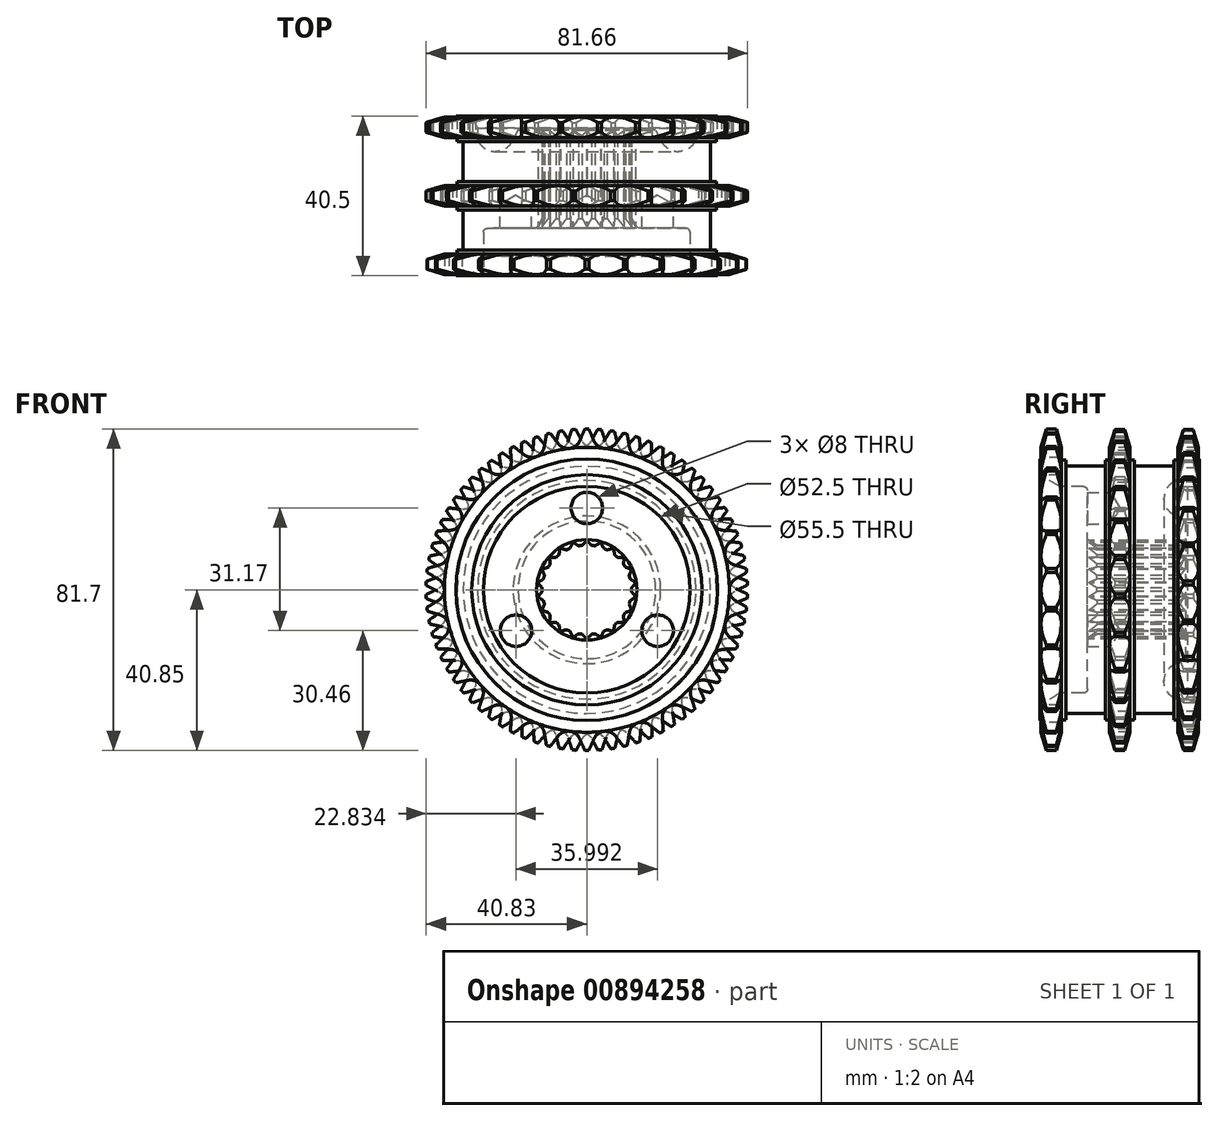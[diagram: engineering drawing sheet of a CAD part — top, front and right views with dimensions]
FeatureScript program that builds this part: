
annotation { "Feature Type Name" : "Feature", "Feature Type Description" : "" }
export const myFeature = defineFeature(function(context is Context, id is Id, definition is map)
    precondition{}
    {
        {
            var Q0;
            Q0=qCreatedBy(makeId("Right.planeOp"),FACE);
            var sketch = newSketch(context, id + "F0", { "sketchPlane" : qUnion([Q0])});
            skLineSegment(sketch, "E0", {"start": v(0, 0) * mm, "end": v(40.5, 0) * mm, "construction": true});
            skLineSegment(sketch, "E1", {"start": v(0, 29.25) * mm, "end": v(0, 33.25) * mm});
            skLineSegment(sketch, "E2", {"start": v(0, 33.25) * mm, "end": v(0.25, 33.25) * mm});
            skLineSegment(sketch, "E3", {"start": v(0.25, 33.25) * mm, "end": v(0.25, 36.2) * mm});
            skLineSegment(sketch, "E4", {"start": v(40.5, 29.25) * mm, "end": v(40.5, 33.25) * mm});
            skLineSegment(sketch, "E5", {"start": v(40.5, 33.25) * mm, "end": v(40.25, 33.25) * mm});
            skLineSegment(sketch, "E6", {"start": v(40.25, 33.25) * mm, "end": v(40.25, 36.2) * mm});
            skLineSegment(sketch, "E7", {"start": v(5, 26.25) * mm, "end": v(0, 29.25) * mm});
            skLineSegment(sketch, "E8", {"start": v(5, 26.25) * mm, "end": v(11, 26.25) * mm});
            skLineSegment(sketch, "E9", {"start": v(12, 25.25) * mm, "end": v(12, 12.75) * mm});
            skLineSegment(sketch, "E10", {"start": v(14.5, 11.35) * mm, "end": v(12, 12.75) * mm});
            skLineSegment(sketch, "E11", {"start": v(37, 17.5) * mm, "end": v(37, 12.75) * mm});
            skLineSegment(sketch, "E12", {"start": v(37, 12.75) * mm, "end": v(35.6, 11.35) * mm});
            skLineSegment(sketch, "E13", {"start": v(14.5, 11.35) * mm, "end": v(35.6, 11.35) * mm});
            skLineSegment(sketch, "E14", {"start": v(40.5, 29.25) * mm, "end": v(37.5, 27.75) * mm});
            skLineSegment(sketch, "E15", {"start": v(34.5, 27.75) * mm, "end": v(37.5, 27.75) * mm});
            skArc(sketch, "E16", {"start": v(34.5, 27.75) * mm, "mid": v(31.5, 23.25) * mm, "end": v(34.5, 18.75) * mm});
            skLineSegment(sketch, "E17", {"start": v(34.5, 18.75) * mm, "end": v(37, 17.5) * mm});
            skLineSegment(sketch, "E18", {"start": v(38.9, 40.85) * mm, "end": v(36.4, 40.85) * mm});
            skLineSegment(sketch, "E19", {"start": v(1.6, 40.85) * mm, "end": v(4.1, 40.85) * mm});
            skLineSegment(sketch, "E20", {"start": v(21.5, 40.85) * mm, "end": v(19, 40.85) * mm});
            skLineSegment(sketch, "E21", {"start": v(36.4, 40.85) * mm, "end": v(35.05, 36.2) * mm});
            skLineSegment(sketch, "E22", {"start": v(38.9, 40.85) * mm, "end": v(40.25, 36.2) * mm});
            skLineSegment(sketch, "E23", {"start": v(19, 40.85) * mm, "end": v(17.65, 36.2) * mm});
            skLineSegment(sketch, "E24", {"start": v(21.5, 40.85) * mm, "end": v(22.85, 36.2) * mm});
            skLineSegment(sketch, "E25", {"start": v(1.6, 40.85) * mm, "end": v(0.25, 36.2) * mm});
            skLineSegment(sketch, "E26", {"start": v(4.1, 40.85) * mm, "end": v(5.45, 36.2) * mm});
            skLineSegment(sketch, "E27", {"start": v(35.05, 33) * mm, "end": v(34, 33) * mm});
            skLineSegment(sketch, "E28", {"start": v(23.9, 33) * mm, "end": v(22.85, 33) * mm});
            skLineSegment(sketch, "E29", {"start": v(17.65, 33) * mm, "end": v(16.6, 33) * mm});
            skLineSegment(sketch, "E30", {"start": v(6.5, 33) * mm, "end": v(5.45, 33) * mm});
            skLineSegment(sketch, "E31", {"start": v(5.45, 36.2) * mm, "end": v(5.45, 33) * mm});
            skLineSegment(sketch, "E32", {"start": v(17.65, 36.2) * mm, "end": v(17.65, 33) * mm});
            skLineSegment(sketch, "E33", {"start": v(22.85, 36.2) * mm, "end": v(22.85, 33) * mm});
            skLineSegment(sketch, "E34", {"start": v(35.05, 36.2) * mm, "end": v(35.05, 33) * mm});
            skLineSegment(sketch, "E35", {"start": v(23.9, 33) * mm, "end": v(23.9, 31.4) * mm});
            skLineSegment(sketch, "E36", {"start": v(16.6, 33) * mm, "end": v(16.6, 31.4) * mm});
            skLineSegment(sketch, "E37", {"start": v(34, 33) * mm, "end": v(34, 31.4) * mm});
            skLineSegment(sketch, "E38", {"start": v(6.5, 33) * mm, "end": v(6.5, 31.4) * mm});
            skLineSegment(sketch, "E39", {"start": v(23.9, 31.4) * mm, "end": v(34, 31.4) * mm});
            skLineSegment(sketch, "E40", {"start": v(16.6, 31.4) * mm, "end": v(6.5, 31.4) * mm});
            skLineSegment(sketch, "E41", {"start": v(0, 29.25) * mm, "end": v(0, 0) * mm, "construction": true});
            skLineSegment(sketch, "E42", {"start": v(0.25, 36.2) * mm, "end": v(5.45, 36.2) * mm, "construction": true});
            skLineSegment(sketch, "E43", {"start": v(17.65, 36.2) * mm, "end": v(22.85, 36.2) * mm, "construction": true});
            skLineSegment(sketch, "E44", {"start": v(35.05, 36.2) * mm, "end": v(40.25, 36.2) * mm, "construction": true});
            skLineSegment(sketch, "E45", {"start": v(4.1, 40.85) * mm, "end": v(19, 40.85) * mm, "construction": true});
            skLineSegment(sketch, "E46", {"start": v(21.5, 40.85) * mm, "end": v(36.4, 40.85) * mm, "construction": true});
            skPoint(sketch, "E47.visualSharp", {"position": v(12, 26.25) * mm});
            skArc(sketch, "E47.filletArc", {"start": v(12, 25.25) * mm, "mid": v(11.7, 25.96) * mm, "end": v(11, 26.25) * mm});
            skSolve(sketch);
        }
        {
            var Q0;
            Q0=makeQuery(id+"F0.imprint","IMPRINT",FACE,{"disambiguationData":[TD([[makeQuery(id+"F0.imprint","IMPRINT",EDGE,{"derivedFrom":sQuery(id+"F0.wireOp",EDGE,"E1")}),-1.0]])]});
            var Q1;
            Q1=sQuery(id+"F0.wireOp",EDGE,"E0");
            revolve(context, id + "F1", {"surfaceOperationType" : NewSurfaceOperationType.NEW, "entities" : qUnion([Q0]), "axis" : qUnion([Q1]), "revolveType" : RevolveType.FULL});
        }
        {
            var Q0;
            Q0=makeQuery(id+"F1.opRevolve","SWEPT_FACE",FACE,{"disambiguationData":[OSD([sQuery(id+"F0.wireOp",EDGE,"E9")])]});
            var sketch = newSketch(context, id + "F2", { "sketchPlane" : qUnion([Q0])});
            skCircle(sketch, "E48", {"center": v(0, 20.78) * mm, "radius": 4 * mm});
            skLineSegment(sketch, "E49", {"start": v(0, 0) * mm, "end": v(0, 20.78) * mm, "construction": true});
            skCircle(sketch, "E50.1.0", {"center": v(-18, -10.39) * mm, "radius": 4 * mm});
            skCircle(sketch, "E50.2.0", {"center": v(18, -10.4) * mm, "radius": 4 * mm});
            skPoint(sketch, "E50.center", {"position": v(0, 0) * mm});
            skSolve(sketch);
        }
        {
            var Q0;
            Q0=sQuery(id+"F2.wireOp",VERTEX,"E49.end");
            var Q1;
            Q1=sQuery(id+"F2.wireOp",VERTEX,"E50.2.0.center");
            var Q2;
            Q2=sQuery(id+"F2.wireOp",VERTEX,"E50.1.0.center");
            var Q3;
            Q3=makeQuery(id+"F1.opRevolve","SWEPT_BODY",BODY,{"disambiguationData":[OSD([sQuery(id+"F0.wireOp",EDGE,"E1"),sQuery(id+"F0.wireOp",EDGE,"E2"),sQuery(id+"F0.wireOp",EDGE,"E3"),sQuery(id+"F0.wireOp",EDGE,"E4"),sQuery(id+"F0.wireOp",EDGE,"E5"),sQuery(id+"F0.wireOp",EDGE,"E6"),sQuery(id+"F0.wireOp",EDGE,"E7"),sQuery(id+"F0.wireOp",EDGE,"E8"),sQuery(id+"F0.wireOp",EDGE,"E9"),sQuery(id+"F0.wireOp",EDGE,"E10"),sQuery(id+"F0.wireOp",EDGE,"E11"),sQuery(id+"F0.wireOp",EDGE,"E12"),sQuery(id+"F0.wireOp",EDGE,"E13"),sQuery(id+"F0.wireOp",EDGE,"E14"),sQuery(id+"F0.wireOp",EDGE,"E15"),sQuery(id+"F0.wireOp",EDGE,"E16"),sQuery(id+"F0.wireOp",EDGE,"E17"),sQuery(id+"F0.wireOp",EDGE,"E18"),sQuery(id+"F0.wireOp",EDGE,"E19"),sQuery(id+"F0.wireOp",EDGE,"E20"),sQuery(id+"F0.wireOp",EDGE,"E21"),sQuery(id+"F0.wireOp",EDGE,"E22"),sQuery(id+"F0.wireOp",EDGE,"E23"),sQuery(id+"F0.wireOp",EDGE,"E24"),sQuery(id+"F0.wireOp",EDGE,"E25"),sQuery(id+"F0.wireOp",EDGE,"E26"),sQuery(id+"F0.wireOp",EDGE,"E27"),sQuery(id+"F0.wireOp",EDGE,"E28"),sQuery(id+"F0.wireOp",EDGE,"E29"),sQuery(id+"F0.wireOp",EDGE,"E30"),sQuery(id+"F0.wireOp",EDGE,"E31"),sQuery(id+"F0.wireOp",EDGE,"E32"),sQuery(id+"F0.wireOp",EDGE,"E33"),sQuery(id+"F0.wireOp",EDGE,"E34"),sQuery(id+"F0.wireOp",EDGE,"E35"),sQuery(id+"F0.wireOp",EDGE,"E36"),sQuery(id+"F0.wireOp",EDGE,"E37"),sQuery(id+"F0.wireOp",EDGE,"E38"),sQuery(id+"F0.wireOp",EDGE,"E39"),sQuery(id+"F0.wireOp",EDGE,"E40")])]});
            hole(context, id + "F3", {"style" : HoleStyle.SIMPLE, "endStyle" : HoleEndStyle.BLIND, "holeDiameter" : 8 * mm, "majorDiameter" : 5 * mm, "holeDepth" : 6 * mm, "isTappedThrough" : true, "tappedDepth" : 12 * mm, "tapClearance" : 3, "locations" : qUnion([Q0, Q1, Q2]), "scope" : qUnion([Q3]), "startStyle" : HoleStartStyle.SKETCH});
        }
        {
            var Q0;
            Q0=makeQuery(id+"F1.opRevolve","SWEPT_FACE",FACE,{"disambiguationData":[OSD([sQuery(id+"F0.wireOp",EDGE,"E9")])]});
            var sketch = newSketch(context, id + "F4", { "sketchPlane" : qUnion([Q0])});
            skArc(sketch, "E51", {"start": v(0.05, 12.5) * mm, "mid": v(0.03, 12.5) * mm, "end": v(0, 12.5) * mm});
            skArc(sketch, "E52", {"start": v(1.62, 11.23) * mm, "mid": v(1.4, 11.26) * mm, "end": v(1.17, 11.29) * mm});
            skLineSegment(sketch, "E53", {"start": v(1.17, 11.29) * mm, "end": v(0.05, 12.5) * mm});
            skArc(sketch, "E54", {"start": v(0, 12.5) * mm, "mid": v(-0.03, 12.5) * mm, "end": v(-0.05, 12.5) * mm});
            skArc(sketch, "E55", {"start": v(-1.17, 11.29) * mm, "mid": v(-1.4, 11.26) * mm, "end": v(-1.62, 11.23) * mm});
            skLineSegment(sketch, "E56", {"start": v(-1.17, 11.29) * mm, "end": v(-0.05, 12.5) * mm});
            skArc(sketch, "E57", {"start": v(-3.47, 12) * mm, "mid": v(-3.5, 12) * mm, "end": v(-3.52, 12) * mm});
            skArc(sketch, "E58", {"start": v(-1.62, 11.23) * mm, "mid": v(-1.84, 11.2) * mm, "end": v(-2.06, 11.16) * mm});
            skLineSegment(sketch, "E59", {"start": v(-2.06, 11.16) * mm, "end": v(-3.47, 12) * mm});
            skArc(sketch, "E60", {"start": v(-3.52, 12) * mm, "mid": v(-3.55, 11.99) * mm, "end": v(-3.57, 11.98) * mm});
            skArc(sketch, "E61", {"start": v(-4.3, 10.5) * mm, "mid": v(-4.5, 10.42) * mm, "end": v(-4.71, 10.32) * mm});
            skLineSegment(sketch, "E62", {"start": v(-4.3, 10.5) * mm, "end": v(-3.57, 11.98) * mm});
            skArc(sketch, "E63", {"start": v(-6.72, 10.54) * mm, "mid": v(-6.74, 10.53) * mm, "end": v(-6.76, 10.52) * mm});
            skArc(sketch, "E64", {"start": v(-4.71, 10.32) * mm, "mid": v(-4.92, 10.23) * mm, "end": v(-5.12, 10.13) * mm});
            skLineSegment(sketch, "E65", {"start": v(-5.12, 10.13) * mm, "end": v(-6.72, 10.54) * mm});
            skArc(sketch, "E66", {"start": v(-6.76, 10.52) * mm, "mid": v(-6.78, 10.5) * mm, "end": v(-6.8, 10.49) * mm});
            skArc(sketch, "E67", {"start": v(-7.09, 8.87) * mm, "mid": v(-7.26, 8.72) * mm, "end": v(-7.43, 8.58) * mm});
            skLineSegment(sketch, "E68", {"start": v(-7.09, 8.87) * mm, "end": v(-6.8, 10.49) * mm});
            skArc(sketch, "E69", {"start": v(-9.41, 8.22) * mm, "mid": v(-9.43, 8.2) * mm, "end": v(-9.45, 8.19) * mm});
            skArc(sketch, "E70", {"start": v(-7.43, 8.58) * mm, "mid": v(-7.6, 8.43) * mm, "end": v(-7.77, 8.28) * mm});
            skLineSegment(sketch, "E71", {"start": v(-7.77, 8.28) * mm, "end": v(-9.41, 8.22) * mm});
            skArc(sketch, "E72", {"start": v(-9.45, 8.19) * mm, "mid": v(-9.46, 8.17) * mm, "end": v(-9.48, 8.15) * mm});
            skArc(sketch, "E73", {"start": v(-9.3, 6.51) * mm, "mid": v(-9.42, 6.32) * mm, "end": v(-9.55, 6.14) * mm});
            skLineSegment(sketch, "E74", {"start": v(-9.3, 6.51) * mm, "end": v(-9.48, 8.15) * mm});
            skArc(sketch, "E75", {"start": v(-11.35, 5.24) * mm, "mid": v(-11.36, 5.22) * mm, "end": v(-11.37, 5.2) * mm});
            skArc(sketch, "E76", {"start": v(-9.55, 6.14) * mm, "mid": v(-9.67, 5.95) * mm, "end": v(-9.78, 5.75) * mm});
            skLineSegment(sketch, "E77", {"start": v(-9.78, 5.75) * mm, "end": v(-11.35, 5.24) * mm});
            skArc(sketch, "E78", {"start": v(-11.37, 5.2) * mm, "mid": v(-11.38, 5.17) * mm, "end": v(-11.4, 5.15) * mm});
            skArc(sketch, "E79", {"start": v(-10.75, 3.63) * mm, "mid": v(-10.82, 3.41) * mm, "end": v(-10.9, 3.2) * mm});
            skLineSegment(sketch, "E80", {"start": v(-10.75, 3.63) * mm, "end": v(-11.4, 5.15) * mm});
            skArc(sketch, "E81", {"start": v(-12.37, 1.83) * mm, "mid": v(-12.37, 1.8) * mm, "end": v(-12.37, 1.78) * mm});
            skArc(sketch, "E82", {"start": v(-10.9, 3.2) * mm, "mid": v(-10.95, 2.98) * mm, "end": v(-11, 2.76) * mm});
            skLineSegment(sketch, "E83", {"start": v(-11, 2.76) * mm, "end": v(-12.37, 1.83) * mm});
            skArc(sketch, "E84", {"start": v(-12.37, 1.78) * mm, "mid": v(-12.38, 1.75) * mm, "end": v(-12.38, 1.73) * mm});
            skArc(sketch, "E85", {"start": v(-11.34, 0.45) * mm, "mid": v(-11.35, 0.23) * mm, "end": v(-11.35, 0) * mm});
            skLineSegment(sketch, "E86", {"start": v(-11.34, 0.45) * mm, "end": v(-12.38, 1.73) * mm});
            skArc(sketch, "E87", {"start": v(-12.38, -1.73) * mm, "mid": v(-12.38, -1.75) * mm, "end": v(-12.37, -1.78) * mm});
            skArc(sketch, "E88", {"start": v(-11.35, 0) * mm, "mid": v(-11.35, -0.23) * mm, "end": v(-11.34, -0.45) * mm});
            skLineSegment(sketch, "E89", {"start": v(-11.34, -0.45) * mm, "end": v(-12.38, -1.73) * mm});
            skArc(sketch, "E90", {"start": v(-12.37, -1.78) * mm, "mid": v(-12.37, -1.8) * mm, "end": v(-12.37, -1.83) * mm});
            skArc(sketch, "E91", {"start": v(-11, -2.76) * mm, "mid": v(-10.95, -2.98) * mm, "end": v(-10.9, -3.2) * mm});
            skLineSegment(sketch, "E92", {"start": v(-11, -2.76) * mm, "end": v(-12.37, -1.83) * mm});
            skArc(sketch, "E93", {"start": v(-11.4, -5.15) * mm, "mid": v(-11.38, -5.17) * mm, "end": v(-11.37, -5.2) * mm});
            skArc(sketch, "E94", {"start": v(-10.9, -3.2) * mm, "mid": v(-10.82, -3.41) * mm, "end": v(-10.75, -3.63) * mm});
            skLineSegment(sketch, "E95", {"start": v(-10.75, -3.63) * mm, "end": v(-11.4, -5.15) * mm});
            skArc(sketch, "E96", {"start": v(-11.37, -5.2) * mm, "mid": v(-11.36, -5.22) * mm, "end": v(-11.35, -5.24) * mm});
            skArc(sketch, "E97", {"start": v(-9.78, -5.75) * mm, "mid": v(-9.67, -5.95) * mm, "end": v(-9.55, -6.14) * mm});
            skLineSegment(sketch, "E98", {"start": v(-9.78, -5.75) * mm, "end": v(-11.35, -5.24) * mm});
            skArc(sketch, "E99", {"start": v(-9.48, -8.15) * mm, "mid": v(-9.46, -8.17) * mm, "end": v(-9.45, -8.19) * mm});
            skArc(sketch, "E100", {"start": v(-9.55, -6.14) * mm, "mid": v(-9.42, -6.32) * mm, "end": v(-9.3, -6.51) * mm});
            skLineSegment(sketch, "E101", {"start": v(-9.3, -6.51) * mm, "end": v(-9.48, -8.15) * mm});
            skArc(sketch, "E102", {"start": v(-9.45, -8.19) * mm, "mid": v(-9.43, -8.2) * mm, "end": v(-9.41, -8.22) * mm});
            skArc(sketch, "E103", {"start": v(-7.77, -8.28) * mm, "mid": v(-7.6, -8.43) * mm, "end": v(-7.43, -8.58) * mm});
            skLineSegment(sketch, "E104", {"start": v(-7.77, -8.28) * mm, "end": v(-9.41, -8.22) * mm});
            skArc(sketch, "E105", {"start": v(-6.8, -10.49) * mm, "mid": v(-6.78, -10.5) * mm, "end": v(-6.76, -10.52) * mm});
            skArc(sketch, "E106", {"start": v(-7.43, -8.58) * mm, "mid": v(-7.26, -8.72) * mm, "end": v(-7.09, -8.87) * mm});
            skLineSegment(sketch, "E107", {"start": v(-7.09, -8.87) * mm, "end": v(-6.8, -10.49) * mm});
            skArc(sketch, "E108", {"start": v(-6.76, -10.52) * mm, "mid": v(-6.74, -10.53) * mm, "end": v(-6.72, -10.54) * mm});
            skArc(sketch, "E109", {"start": v(-5.12, -10.13) * mm, "mid": v(-4.92, -10.23) * mm, "end": v(-4.71, -10.32) * mm});
            skLineSegment(sketch, "E110", {"start": v(-5.12, -10.13) * mm, "end": v(-6.72, -10.54) * mm});
            skArc(sketch, "E111", {"start": v(-3.57, -11.98) * mm, "mid": v(-3.55, -11.99) * mm, "end": v(-3.52, -12) * mm});
            skArc(sketch, "E112", {"start": v(-4.71, -10.32) * mm, "mid": v(-4.5, -10.42) * mm, "end": v(-4.3, -10.5) * mm});
            skLineSegment(sketch, "E113", {"start": v(-4.3, -10.5) * mm, "end": v(-3.57, -11.98) * mm});
            skArc(sketch, "E114", {"start": v(-3.52, -12) * mm, "mid": v(-3.5, -12) * mm, "end": v(-3.47, -12) * mm});
            skArc(sketch, "E115", {"start": v(-2.06, -11.16) * mm, "mid": v(-1.84, -11.2) * mm, "end": v(-1.62, -11.23) * mm});
            skLineSegment(sketch, "E116", {"start": v(-2.06, -11.16) * mm, "end": v(-3.47, -12) * mm});
            skArc(sketch, "E117", {"start": v(-0.05, -12.5) * mm, "mid": v(-0.03, -12.5) * mm, "end": v(0, -12.5) * mm});
            skArc(sketch, "E118", {"start": v(-1.62, -11.23) * mm, "mid": v(-1.4, -11.26) * mm, "end": v(-1.17, -11.29) * mm});
            skLineSegment(sketch, "E119", {"start": v(-1.17, -11.29) * mm, "end": v(-0.05, -12.5) * mm});
            skArc(sketch, "E120", {"start": v(0, -12.5) * mm, "mid": v(0.03, -12.5) * mm, "end": v(0.05, -12.5) * mm});
            skArc(sketch, "E121", {"start": v(1.17, -11.29) * mm, "mid": v(1.4, -11.26) * mm, "end": v(1.62, -11.23) * mm});
            skLineSegment(sketch, "E122", {"start": v(1.17, -11.29) * mm, "end": v(0.05, -12.5) * mm});
            skArc(sketch, "E123", {"start": v(3.47, -12) * mm, "mid": v(3.5, -12) * mm, "end": v(3.52, -12) * mm});
            skArc(sketch, "E124", {"start": v(1.62, -11.23) * mm, "mid": v(1.84, -11.2) * mm, "end": v(2.06, -11.16) * mm});
            skLineSegment(sketch, "E125", {"start": v(2.06, -11.16) * mm, "end": v(3.47, -12) * mm});
            skArc(sketch, "E126", {"start": v(3.52, -12) * mm, "mid": v(3.55, -11.99) * mm, "end": v(3.57, -11.98) * mm});
            skArc(sketch, "E127", {"start": v(4.3, -10.5) * mm, "mid": v(4.5, -10.42) * mm, "end": v(4.71, -10.32) * mm});
            skLineSegment(sketch, "E128", {"start": v(4.3, -10.5) * mm, "end": v(3.57, -11.98) * mm});
            skArc(sketch, "E129", {"start": v(6.72, -10.54) * mm, "mid": v(6.74, -10.53) * mm, "end": v(6.76, -10.52) * mm});
            skArc(sketch, "E130", {"start": v(4.71, -10.32) * mm, "mid": v(4.92, -10.23) * mm, "end": v(5.12, -10.13) * mm});
            skLineSegment(sketch, "E131", {"start": v(5.12, -10.13) * mm, "end": v(6.72, -10.54) * mm});
            skArc(sketch, "E132", {"start": v(6.76, -10.52) * mm, "mid": v(6.78, -10.5) * mm, "end": v(6.8, -10.49) * mm});
            skArc(sketch, "E133", {"start": v(7.09, -8.87) * mm, "mid": v(7.26, -8.72) * mm, "end": v(7.43, -8.58) * mm});
            skLineSegment(sketch, "E134", {"start": v(7.09, -8.87) * mm, "end": v(6.8, -10.49) * mm});
            skArc(sketch, "E135", {"start": v(9.41, -8.22) * mm, "mid": v(9.43, -8.2) * mm, "end": v(9.45, -8.19) * mm});
            skArc(sketch, "E136", {"start": v(7.43, -8.58) * mm, "mid": v(7.6, -8.43) * mm, "end": v(7.77, -8.28) * mm});
            skLineSegment(sketch, "E137", {"start": v(7.77, -8.28) * mm, "end": v(9.41, -8.22) * mm});
            skArc(sketch, "E138", {"start": v(9.45, -8.19) * mm, "mid": v(9.46, -8.17) * mm, "end": v(9.48, -8.15) * mm});
            skArc(sketch, "E139", {"start": v(9.3, -6.51) * mm, "mid": v(9.42, -6.32) * mm, "end": v(9.55, -6.14) * mm});
            skLineSegment(sketch, "E140", {"start": v(9.3, -6.51) * mm, "end": v(9.48, -8.15) * mm});
            skArc(sketch, "E141", {"start": v(11.35, -5.24) * mm, "mid": v(11.36, -5.22) * mm, "end": v(11.37, -5.2) * mm});
            skArc(sketch, "E142", {"start": v(9.55, -6.14) * mm, "mid": v(9.67, -5.95) * mm, "end": v(9.78, -5.75) * mm});
            skLineSegment(sketch, "E143", {"start": v(9.78, -5.75) * mm, "end": v(11.35, -5.24) * mm});
            skArc(sketch, "E144", {"start": v(11.37, -5.2) * mm, "mid": v(11.38, -5.17) * mm, "end": v(11.4, -5.15) * mm});
            skArc(sketch, "E145", {"start": v(10.75, -3.63) * mm, "mid": v(10.82, -3.41) * mm, "end": v(10.9, -3.2) * mm});
            skLineSegment(sketch, "E146", {"start": v(10.75, -3.63) * mm, "end": v(11.4, -5.15) * mm});
            skArc(sketch, "E147", {"start": v(12.37, -1.83) * mm, "mid": v(12.37, -1.8) * mm, "end": v(12.37, -1.78) * mm});
            skArc(sketch, "E148", {"start": v(10.9, -3.2) * mm, "mid": v(10.95, -2.98) * mm, "end": v(11, -2.76) * mm});
            skLineSegment(sketch, "E149", {"start": v(11, -2.76) * mm, "end": v(12.37, -1.83) * mm});
            skArc(sketch, "E150", {"start": v(12.37, -1.78) * mm, "mid": v(12.38, -1.75) * mm, "end": v(12.38, -1.73) * mm});
            skArc(sketch, "E151", {"start": v(11.34, -0.45) * mm, "mid": v(11.35, -0.23) * mm, "end": v(11.35, 0) * mm});
            skLineSegment(sketch, "E152", {"start": v(11.34, -0.45) * mm, "end": v(12.38, -1.73) * mm});
            skArc(sketch, "E153", {"start": v(12.38, 1.73) * mm, "mid": v(12.38, 1.75) * mm, "end": v(12.37, 1.78) * mm});
            skArc(sketch, "E154", {"start": v(11.35, 0) * mm, "mid": v(11.35, 0.23) * mm, "end": v(11.34, 0.45) * mm});
            skLineSegment(sketch, "E155", {"start": v(11.34, 0.45) * mm, "end": v(12.38, 1.73) * mm});
            skArc(sketch, "E156", {"start": v(12.37, 1.78) * mm, "mid": v(12.37, 1.8) * mm, "end": v(12.37, 1.83) * mm});
            skArc(sketch, "E157", {"start": v(11, 2.76) * mm, "mid": v(10.95, 2.98) * mm, "end": v(10.9, 3.2) * mm});
            skLineSegment(sketch, "E158", {"start": v(11, 2.76) * mm, "end": v(12.37, 1.83) * mm});
            skArc(sketch, "E159", {"start": v(11.4, 5.15) * mm, "mid": v(11.38, 5.17) * mm, "end": v(11.37, 5.2) * mm});
            skArc(sketch, "E160", {"start": v(10.9, 3.2) * mm, "mid": v(10.82, 3.41) * mm, "end": v(10.75, 3.63) * mm});
            skLineSegment(sketch, "E161", {"start": v(10.75, 3.63) * mm, "end": v(11.4, 5.15) * mm});
            skArc(sketch, "E162", {"start": v(11.37, 5.2) * mm, "mid": v(11.36, 5.22) * mm, "end": v(11.35, 5.24) * mm});
            skArc(sketch, "E163", {"start": v(9.78, 5.75) * mm, "mid": v(9.67, 5.95) * mm, "end": v(9.55, 6.14) * mm});
            skLineSegment(sketch, "E164", {"start": v(9.78, 5.75) * mm, "end": v(11.35, 5.24) * mm});
            skArc(sketch, "E165", {"start": v(9.48, 8.15) * mm, "mid": v(9.46, 8.17) * mm, "end": v(9.45, 8.19) * mm});
            skArc(sketch, "E166", {"start": v(9.55, 6.14) * mm, "mid": v(9.42, 6.32) * mm, "end": v(9.3, 6.51) * mm});
            skLineSegment(sketch, "E167", {"start": v(9.3, 6.51) * mm, "end": v(9.48, 8.15) * mm});
            skArc(sketch, "E168", {"start": v(9.45, 8.19) * mm, "mid": v(9.43, 8.2) * mm, "end": v(9.41, 8.22) * mm});
            skArc(sketch, "E169", {"start": v(7.77, 8.28) * mm, "mid": v(7.6, 8.43) * mm, "end": v(7.43, 8.58) * mm});
            skLineSegment(sketch, "E170", {"start": v(7.77, 8.28) * mm, "end": v(9.41, 8.22) * mm});
            skArc(sketch, "E171", {"start": v(6.8, 10.49) * mm, "mid": v(6.78, 10.5) * mm, "end": v(6.76, 10.52) * mm});
            skArc(sketch, "E172", {"start": v(7.43, 8.58) * mm, "mid": v(7.26, 8.72) * mm, "end": v(7.09, 8.87) * mm});
            skLineSegment(sketch, "E173", {"start": v(7.09, 8.87) * mm, "end": v(6.8, 10.49) * mm});
            skArc(sketch, "E174", {"start": v(6.76, 10.52) * mm, "mid": v(6.74, 10.53) * mm, "end": v(6.72, 10.54) * mm});
            skArc(sketch, "E175", {"start": v(5.12, 10.13) * mm, "mid": v(4.92, 10.23) * mm, "end": v(4.71, 10.32) * mm});
            skLineSegment(sketch, "E176", {"start": v(5.12, 10.13) * mm, "end": v(6.72, 10.54) * mm});
            skArc(sketch, "E177", {"start": v(3.57, 11.98) * mm, "mid": v(3.55, 11.99) * mm, "end": v(3.52, 12) * mm});
            skArc(sketch, "E178", {"start": v(4.71, 10.32) * mm, "mid": v(4.5, 10.42) * mm, "end": v(4.3, 10.5) * mm});
            skLineSegment(sketch, "E179", {"start": v(4.3, 10.5) * mm, "end": v(3.57, 11.98) * mm});
            skArc(sketch, "E180", {"start": v(3.52, 12) * mm, "mid": v(3.5, 12) * mm, "end": v(3.47, 12) * mm});
            skArc(sketch, "E181", {"start": v(2.06, 11.16) * mm, "mid": v(1.84, 11.2) * mm, "end": v(1.62, 11.23) * mm});
            skLineSegment(sketch, "E182", {"start": v(2.06, 11.16) * mm, "end": v(3.47, 12) * mm});
            skSolve(sketch);
        }
        {
            var Q0;
            Q0=makeQuery(id+"F4.imprint","IMPRINT",FACE,{"disambiguationData":[TD([[makeQuery(id+"F4.imprint","IMPRINT",EDGE,{"derivedFrom":sQuery(id+"F4.wireOp",EDGE,"E51")}),1.0]])]});
            extrude(context, id + "F5", {"entities" : qUnion([Q0]), "operationType" : NewBodyOperationType.REMOVE, "endBound" : BoundingType.THROUGH_ALL, "oppositeDirection" : true, "depth" : 25 * mm, "offsetDistance" : 25 * mm});
        }
        {
            var Q0;
            Q0=makeQuery(id+"F1.opRevolve","SWEPT_FACE",FACE,{"disambiguationData":[OSD([sQuery(id+"F0.wireOp",EDGE,"E3")])]});
            var sketch = newSketch(context, id + "F6", { "sketchPlane" : qUnion([Q0])});
            skArc(sketch, "E183", {"start": v(0.5, 40.85) * mm, "mid": v(0.25, 40.85) * mm, "end": v(0, 40.85) * mm});
            skArc(sketch, "E184", {"start": v(1.82, 37.83) * mm, "mid": v(2.84, 36.55) * mm, "end": v(4.36, 35.94) * mm});
            skLineSegment(sketch, "E185", {"start": v(0.5, 40.85) * mm, "end": v(1.82, 37.83) * mm});
            skArc(sketch, "E186", {"start": v(0, 40.85) * mm, "mid": v(-0.25, 40.85) * mm, "end": v(-0.5, 40.85) * mm});
            skArc(sketch, "E187", {"start": v(-4.36, 35.94) * mm, "mid": v(-2.84, 36.55) * mm, "end": v(-1.82, 37.83) * mm});
            skLineSegment(sketch, "E188", {"start": v(-0.5, 40.85) * mm, "end": v(-1.82, 37.83) * mm});
            skArc(sketch, "E189.1.0", {"start": v(-7.3, 37.17) * mm, "mid": v(-6, 36.16) * mm, "end": v(-4.36, 35.94) * mm});
            skLineSegment(sketch, "E189.1.1", {"start": v(-9.29, 39.78) * mm, "end": v(-7.3, 37.17) * mm});
            skArc(sketch, "E189.1.2", {"start": v(-9.29, 39.78) * mm, "mid": v(-9.53, 39.72) * mm, "end": v(-9.78, 39.66) * mm});
            skArc(sketch, "E189.1.3", {"start": v(-9.78, 39.66) * mm, "mid": v(-10.02, 39.6) * mm, "end": v(-10.26, 39.54) * mm});
            skLineSegment(sketch, "E189.1.4", {"start": v(-10.26, 39.54) * mm, "end": v(-10.82, 36.3) * mm});
            skArc(sketch, "E189.1.5", {"start": v(-12.84, 33.85) * mm, "mid": v(-11.5, 34.8) * mm, "end": v(-10.82, 36.3) * mm});
            skArc(sketch, "E189.2.0", {"start": v(-15.97, 34.34) * mm, "mid": v(-14.47, 33.68) * mm, "end": v(-12.84, 33.85) * mm});
            skLineSegment(sketch, "E189.2.1", {"start": v(-18.54, 36.4) * mm, "end": v(-15.97, 34.34) * mm});
            skArc(sketch, "E189.2.2", {"start": v(-18.54, 36.4) * mm, "mid": v(-18.76, 36.29) * mm, "end": v(-18.98, 36.17) * mm});
            skArc(sketch, "E189.2.3", {"start": v(-18.98, 36.17) * mm, "mid": v(-19.2, 36.05) * mm, "end": v(-19.43, 35.94) * mm});
            skLineSegment(sketch, "E189.2.4", {"start": v(-19.43, 35.94) * mm, "end": v(-19.19, 32.65) * mm});
            skArc(sketch, "E189.2.5", {"start": v(-20.56, 29.8) * mm, "mid": v(-19.5, 31.04) * mm, "end": v(-19.19, 32.65) * mm});
            skArc(sketch, "E189.3.0", {"start": v(-23.73, 29.52) * mm, "mid": v(-22.1, 29.24) * mm, "end": v(-20.56, 29.8) * mm});
            skLineSegment(sketch, "E189.3.1", {"start": v(-26.71, 30.9) * mm, "end": v(-23.73, 29.52) * mm});
            skArc(sketch, "E189.3.2", {"start": v(-26.71, 30.9) * mm, "mid": v(-26.9, 30.74) * mm, "end": v(-27.09, 30.58) * mm});
            skArc(sketch, "E189.3.3", {"start": v(-27.09, 30.58) * mm, "mid": v(-27.28, 30.41) * mm, "end": v(-27.46, 30.24) * mm});
            skLineSegment(sketch, "E189.3.4", {"start": v(-27.46, 30.24) * mm, "end": v(-26.45, 27.11) * mm});
            skArc(sketch, "E189.3.5", {"start": v(-27.1, 24) * mm, "mid": v(-26.36, 25.47) * mm, "end": v(-26.45, 27.11) * mm});
            skArc(sketch, "E189.4.0", {"start": v(-30.1, 22.99) * mm, "mid": v(-28.46, 23.1) * mm, "end": v(-27.1, 24) * mm});
            skLineSegment(sketch, "E189.4.1", {"start": v(-33.33, 23.62) * mm, "end": v(-30.1, 22.99) * mm});
            skArc(sketch, "E189.4.2", {"start": v(-33.33, 23.62) * mm, "mid": v(-33.48, 23.41) * mm, "end": v(-33.62, 23.2) * mm});
            skArc(sketch, "E189.4.3", {"start": v(-33.62, 23.2) * mm, "mid": v(-33.76, 23) * mm, "end": v(-33.9, 22.8) * mm});
            skLineSegment(sketch, "E189.4.4", {"start": v(-33.9, 22.8) * mm, "end": v(-32.17, 20) * mm});
            skArc(sketch, "E189.4.5", {"start": v(-32.05, 16.82) * mm, "mid": v(-31.69, 18.42) * mm, "end": v(-32.17, 20) * mm});
            skArc(sketch, "E189.5.0", {"start": v(-34.73, 15.11) * mm, "mid": v(-33.16, 15.61) * mm, "end": v(-32.05, 16.82) * mm});
            skLineSegment(sketch, "E189.5.1", {"start": v(-38.02, 14.95) * mm, "end": v(-34.73, 15.11) * mm});
            skArc(sketch, "E189.5.2", {"start": v(-38.02, 14.95) * mm, "mid": v(-38.1, 14.72) * mm, "end": v(-38.2, 14.49) * mm});
            skArc(sketch, "E189.5.3", {"start": v(-38.2, 14.49) * mm, "mid": v(-38.28, 14.25) * mm, "end": v(-38.37, 14.02) * mm});
            skLineSegment(sketch, "E189.5.4", {"start": v(-38.37, 14.02) * mm, "end": v(-36.02, 11.72) * mm});
            skArc(sketch, "E189.5.5", {"start": v(-35.15, 8.66) * mm, "mid": v(-35.18, 10.3) * mm, "end": v(-36.02, 11.72) * mm});
            skArc(sketch, "E189.6.0", {"start": v(-37.34, 6.36) * mm, "mid": v(-35.94, 7.22) * mm, "end": v(-35.15, 8.66) * mm});
            skLineSegment(sketch, "E189.6.1", {"start": v(-40.49, 5.42) * mm, "end": v(-37.34, 6.36) * mm});
            skArc(sketch, "E189.6.2", {"start": v(-40.49, 5.42) * mm, "mid": v(-40.52, 5.17) * mm, "end": v(-40.55, 4.92) * mm});
            skArc(sketch, "E189.6.3", {"start": v(-40.55, 4.92) * mm, "mid": v(-40.58, 4.68) * mm, "end": v(-40.6, 4.43) * mm});
            skLineSegment(sketch, "E189.6.4", {"start": v(-40.6, 4.43) * mm, "end": v(-37.78, 2.76) * mm});
            skArc(sketch, "E189.6.5", {"start": v(-36.2, 0) * mm, "mid": v(-36.62, 1.59) * mm, "end": v(-37.78, 2.76) * mm});
            skArc(sketch, "E189.7.0", {"start": v(-37.78, -2.76) * mm, "mid": v(-36.62, -1.59) * mm, "end": v(-36.2, 0) * mm});
            skLineSegment(sketch, "E189.7.1", {"start": v(-40.6, -4.43) * mm, "end": v(-37.78, -2.76) * mm});
            skArc(sketch, "E189.7.2", {"start": v(-40.6, -4.43) * mm, "mid": v(-40.58, -4.68) * mm, "end": v(-40.55, -4.92) * mm});
            skArc(sketch, "E189.7.3", {"start": v(-40.55, -4.92) * mm, "mid": v(-40.52, -5.17) * mm, "end": v(-40.49, -5.42) * mm});
            skLineSegment(sketch, "E189.7.4", {"start": v(-40.49, -5.42) * mm, "end": v(-37.34, -6.36) * mm});
            skArc(sketch, "E189.7.5", {"start": v(-35.15, -8.66) * mm, "mid": v(-35.94, -7.22) * mm, "end": v(-37.34, -6.36) * mm});
            skArc(sketch, "E189.8.0", {"start": v(-36.02, -11.72) * mm, "mid": v(-35.18, -10.3) * mm, "end": v(-35.15, -8.66) * mm});
            skLineSegment(sketch, "E189.8.1", {"start": v(-38.37, -14.02) * mm, "end": v(-36.02, -11.72) * mm});
            skArc(sketch, "E189.8.2", {"start": v(-38.37, -14.02) * mm, "mid": v(-38.28, -14.25) * mm, "end": v(-38.2, -14.49) * mm});
            skArc(sketch, "E189.8.3", {"start": v(-38.2, -14.49) * mm, "mid": v(-38.1, -14.72) * mm, "end": v(-38.02, -14.95) * mm});
            skLineSegment(sketch, "E189.8.4", {"start": v(-38.02, -14.95) * mm, "end": v(-34.73, -15.11) * mm});
            skArc(sketch, "E189.8.5", {"start": v(-32.05, -16.82) * mm, "mid": v(-33.16, -15.61) * mm, "end": v(-34.73, -15.11) * mm});
            skArc(sketch, "E189.9.0", {"start": v(-32.17, -20) * mm, "mid": v(-31.69, -18.42) * mm, "end": v(-32.05, -16.82) * mm});
            skLineSegment(sketch, "E189.9.1", {"start": v(-33.9, -22.8) * mm, "end": v(-32.17, -20) * mm});
            skArc(sketch, "E189.9.2", {"start": v(-33.9, -22.8) * mm, "mid": v(-33.76, -23) * mm, "end": v(-33.62, -23.2) * mm});
            skArc(sketch, "E189.9.3", {"start": v(-33.62, -23.2) * mm, "mid": v(-33.48, -23.41) * mm, "end": v(-33.33, -23.62) * mm});
            skLineSegment(sketch, "E189.9.4", {"start": v(-33.33, -23.62) * mm, "end": v(-30.1, -22.99) * mm});
            skArc(sketch, "E189.9.5", {"start": v(-27.1, -24) * mm, "mid": v(-28.46, -23.1) * mm, "end": v(-30.1, -22.99) * mm});
            skArc(sketch, "E189.10.0", {"start": v(-26.45, -27.11) * mm, "mid": v(-26.36, -25.47) * mm, "end": v(-27.1, -24) * mm});
            skLineSegment(sketch, "E189.10.1", {"start": v(-27.46, -30.24) * mm, "end": v(-26.45, -27.11) * mm});
            skArc(sketch, "E189.10.2", {"start": v(-27.46, -30.24) * mm, "mid": v(-27.28, -30.41) * mm, "end": v(-27.09, -30.58) * mm});
            skArc(sketch, "E189.10.3", {"start": v(-27.09, -30.58) * mm, "mid": v(-26.9, -30.74) * mm, "end": v(-26.71, -30.9) * mm});
            skLineSegment(sketch, "E189.10.4", {"start": v(-26.71, -30.9) * mm, "end": v(-23.73, -29.52) * mm});
            skArc(sketch, "E189.10.5", {"start": v(-20.56, -29.8) * mm, "mid": v(-22.1, -29.24) * mm, "end": v(-23.73, -29.52) * mm});
            skArc(sketch, "E189.11.0", {"start": v(-19.19, -32.65) * mm, "mid": v(-19.5, -31.04) * mm, "end": v(-20.56, -29.8) * mm});
            skLineSegment(sketch, "E189.11.1", {"start": v(-19.43, -35.94) * mm, "end": v(-19.19, -32.65) * mm});
            skArc(sketch, "E189.11.2", {"start": v(-19.43, -35.94) * mm, "mid": v(-19.2, -36.05) * mm, "end": v(-18.98, -36.17) * mm});
            skArc(sketch, "E189.11.3", {"start": v(-18.98, -36.17) * mm, "mid": v(-18.76, -36.29) * mm, "end": v(-18.54, -36.4) * mm});
            skLineSegment(sketch, "E189.11.4", {"start": v(-18.54, -36.4) * mm, "end": v(-15.97, -34.34) * mm});
            skArc(sketch, "E189.11.5", {"start": v(-12.84, -33.85) * mm, "mid": v(-14.47, -33.68) * mm, "end": v(-15.97, -34.34) * mm});
            skArc(sketch, "E189.12.0", {"start": v(-10.82, -36.3) * mm, "mid": v(-11.5, -34.8) * mm, "end": v(-12.84, -33.85) * mm});
            skLineSegment(sketch, "E189.12.1", {"start": v(-10.26, -39.54) * mm, "end": v(-10.82, -36.3) * mm});
            skArc(sketch, "E189.12.2", {"start": v(-10.26, -39.54) * mm, "mid": v(-10.02, -39.6) * mm, "end": v(-9.78, -39.66) * mm});
            skArc(sketch, "E189.12.3", {"start": v(-9.78, -39.66) * mm, "mid": v(-9.53, -39.72) * mm, "end": v(-9.29, -39.78) * mm});
            skLineSegment(sketch, "E189.12.4", {"start": v(-9.29, -39.78) * mm, "end": v(-7.3, -37.17) * mm});
            skArc(sketch, "E189.12.5", {"start": v(-4.36, -35.94) * mm, "mid": v(-6, -36.16) * mm, "end": v(-7.3, -37.17) * mm});
            skArc(sketch, "E189.13.0", {"start": v(-1.82, -37.83) * mm, "mid": v(-2.84, -36.55) * mm, "end": v(-4.36, -35.94) * mm});
            skLineSegment(sketch, "E189.13.1", {"start": v(-0.5, -40.85) * mm, "end": v(-1.82, -37.83) * mm});
            skArc(sketch, "E189.13.2", {"start": v(-0.5, -40.85) * mm, "mid": v(-0.25, -40.85) * mm, "end": v(0, -40.85) * mm});
            skArc(sketch, "E189.13.3", {"start": v(0, -40.85) * mm, "mid": v(0.25, -40.85) * mm, "end": v(0.5, -40.85) * mm});
            skLineSegment(sketch, "E189.13.4", {"start": v(0.5, -40.85) * mm, "end": v(1.82, -37.83) * mm});
            skArc(sketch, "E189.13.5", {"start": v(4.36, -35.94) * mm, "mid": v(2.84, -36.55) * mm, "end": v(1.82, -37.83) * mm});
            skArc(sketch, "E189.14.0", {"start": v(7.3, -37.17) * mm, "mid": v(6, -36.16) * mm, "end": v(4.36, -35.94) * mm});
            skLineSegment(sketch, "E189.14.1", {"start": v(9.29, -39.78) * mm, "end": v(7.3, -37.17) * mm});
            skArc(sketch, "E189.14.2", {"start": v(9.29, -39.78) * mm, "mid": v(9.53, -39.72) * mm, "end": v(9.78, -39.66) * mm});
            skArc(sketch, "E189.14.3", {"start": v(9.78, -39.66) * mm, "mid": v(10.02, -39.6) * mm, "end": v(10.26, -39.54) * mm});
            skLineSegment(sketch, "E189.14.4", {"start": v(10.26, -39.54) * mm, "end": v(10.82, -36.3) * mm});
            skArc(sketch, "E189.14.5", {"start": v(12.84, -33.85) * mm, "mid": v(11.5, -34.8) * mm, "end": v(10.82, -36.3) * mm});
            skArc(sketch, "E189.15.0", {"start": v(15.97, -34.34) * mm, "mid": v(14.47, -33.68) * mm, "end": v(12.84, -33.85) * mm});
            skLineSegment(sketch, "E189.15.1", {"start": v(18.54, -36.4) * mm, "end": v(15.97, -34.34) * mm});
            skArc(sketch, "E189.15.2", {"start": v(18.54, -36.4) * mm, "mid": v(18.76, -36.29) * mm, "end": v(18.98, -36.17) * mm});
            skArc(sketch, "E189.15.3", {"start": v(18.98, -36.17) * mm, "mid": v(19.2, -36.05) * mm, "end": v(19.43, -35.94) * mm});
            skLineSegment(sketch, "E189.15.4", {"start": v(19.43, -35.94) * mm, "end": v(19.19, -32.65) * mm});
            skArc(sketch, "E189.15.5", {"start": v(20.56, -29.8) * mm, "mid": v(19.5, -31.04) * mm, "end": v(19.19, -32.65) * mm});
            skArc(sketch, "E189.16.0", {"start": v(23.73, -29.52) * mm, "mid": v(22.1, -29.24) * mm, "end": v(20.56, -29.8) * mm});
            skLineSegment(sketch, "E189.16.1", {"start": v(26.71, -30.9) * mm, "end": v(23.73, -29.52) * mm});
            skArc(sketch, "E189.16.2", {"start": v(26.71, -30.9) * mm, "mid": v(26.9, -30.74) * mm, "end": v(27.09, -30.58) * mm});
            skArc(sketch, "E189.16.3", {"start": v(27.09, -30.58) * mm, "mid": v(27.28, -30.41) * mm, "end": v(27.46, -30.24) * mm});
            skLineSegment(sketch, "E189.16.4", {"start": v(27.46, -30.24) * mm, "end": v(26.45, -27.11) * mm});
            skArc(sketch, "E189.16.5", {"start": v(27.1, -24) * mm, "mid": v(26.36, -25.47) * mm, "end": v(26.45, -27.11) * mm});
            skArc(sketch, "E189.17.0", {"start": v(30.1, -22.99) * mm, "mid": v(28.46, -23.1) * mm, "end": v(27.1, -24) * mm});
            skLineSegment(sketch, "E189.17.1", {"start": v(33.33, -23.62) * mm, "end": v(30.1, -22.99) * mm});
            skArc(sketch, "E189.17.2", {"start": v(33.33, -23.62) * mm, "mid": v(33.48, -23.41) * mm, "end": v(33.62, -23.2) * mm});
            skArc(sketch, "E189.17.3", {"start": v(33.62, -23.2) * mm, "mid": v(33.76, -23) * mm, "end": v(33.9, -22.8) * mm});
            skLineSegment(sketch, "E189.17.4", {"start": v(33.9, -22.8) * mm, "end": v(32.17, -20) * mm});
            skArc(sketch, "E189.17.5", {"start": v(32.05, -16.82) * mm, "mid": v(31.69, -18.42) * mm, "end": v(32.17, -20) * mm});
            skArc(sketch, "E189.18.0", {"start": v(34.73, -15.11) * mm, "mid": v(33.16, -15.61) * mm, "end": v(32.05, -16.82) * mm});
            skLineSegment(sketch, "E189.18.1", {"start": v(38.02, -14.95) * mm, "end": v(34.73, -15.11) * mm});
            skArc(sketch, "E189.18.2", {"start": v(38.02, -14.95) * mm, "mid": v(38.1, -14.72) * mm, "end": v(38.2, -14.49) * mm});
            skArc(sketch, "E189.18.3", {"start": v(38.2, -14.49) * mm, "mid": v(38.28, -14.25) * mm, "end": v(38.37, -14.02) * mm});
            skLineSegment(sketch, "E189.18.4", {"start": v(38.37, -14.02) * mm, "end": v(36.02, -11.72) * mm});
            skArc(sketch, "E189.18.5", {"start": v(35.15, -8.66) * mm, "mid": v(35.18, -10.3) * mm, "end": v(36.02, -11.72) * mm});
            skArc(sketch, "E189.19.0", {"start": v(37.34, -6.36) * mm, "mid": v(35.94, -7.22) * mm, "end": v(35.15, -8.66) * mm});
            skLineSegment(sketch, "E189.19.1", {"start": v(40.49, -5.42) * mm, "end": v(37.34, -6.36) * mm});
            skArc(sketch, "E189.19.2", {"start": v(40.49, -5.42) * mm, "mid": v(40.52, -5.17) * mm, "end": v(40.55, -4.92) * mm});
            skArc(sketch, "E189.19.3", {"start": v(40.55, -4.92) * mm, "mid": v(40.58, -4.68) * mm, "end": v(40.6, -4.43) * mm});
            skLineSegment(sketch, "E189.19.4", {"start": v(40.6, -4.43) * mm, "end": v(37.78, -2.76) * mm});
            skArc(sketch, "E189.19.5", {"start": v(36.2, 0) * mm, "mid": v(36.62, -1.59) * mm, "end": v(37.78, -2.76) * mm});
            skArc(sketch, "E189.20.0", {"start": v(37.78, 2.76) * mm, "mid": v(36.62, 1.59) * mm, "end": v(36.2, 0) * mm});
            skLineSegment(sketch, "E189.20.1", {"start": v(40.6, 4.43) * mm, "end": v(37.78, 2.76) * mm});
            skArc(sketch, "E189.20.2", {"start": v(40.6, 4.43) * mm, "mid": v(40.58, 4.68) * mm, "end": v(40.55, 4.92) * mm});
            skArc(sketch, "E189.20.3", {"start": v(40.55, 4.92) * mm, "mid": v(40.52, 5.17) * mm, "end": v(40.49, 5.42) * mm});
            skLineSegment(sketch, "E189.20.4", {"start": v(40.49, 5.42) * mm, "end": v(37.34, 6.36) * mm});
            skArc(sketch, "E189.20.5", {"start": v(35.15, 8.66) * mm, "mid": v(35.94, 7.22) * mm, "end": v(37.34, 6.36) * mm});
            skArc(sketch, "E189.21.0", {"start": v(36.02, 11.72) * mm, "mid": v(35.18, 10.3) * mm, "end": v(35.15, 8.66) * mm});
            skLineSegment(sketch, "E189.21.1", {"start": v(38.37, 14.02) * mm, "end": v(36.02, 11.72) * mm});
            skArc(sketch, "E189.21.2", {"start": v(38.37, 14.02) * mm, "mid": v(38.28, 14.25) * mm, "end": v(38.2, 14.49) * mm});
            skArc(sketch, "E189.21.3", {"start": v(38.2, 14.49) * mm, "mid": v(38.1, 14.72) * mm, "end": v(38.02, 14.95) * mm});
            skLineSegment(sketch, "E189.21.4", {"start": v(38.02, 14.95) * mm, "end": v(34.73, 15.11) * mm});
            skArc(sketch, "E189.21.5", {"start": v(32.05, 16.82) * mm, "mid": v(33.16, 15.61) * mm, "end": v(34.73, 15.11) * mm});
            skArc(sketch, "E189.22.0", {"start": v(32.17, 20) * mm, "mid": v(31.69, 18.42) * mm, "end": v(32.05, 16.82) * mm});
            skLineSegment(sketch, "E189.22.1", {"start": v(33.9, 22.8) * mm, "end": v(32.17, 20) * mm});
            skArc(sketch, "E189.22.2", {"start": v(33.9, 22.8) * mm, "mid": v(33.76, 23) * mm, "end": v(33.62, 23.2) * mm});
            skArc(sketch, "E189.22.3", {"start": v(33.62, 23.2) * mm, "mid": v(33.48, 23.41) * mm, "end": v(33.33, 23.62) * mm});
            skLineSegment(sketch, "E189.22.4", {"start": v(33.33, 23.62) * mm, "end": v(30.1, 22.99) * mm});
            skArc(sketch, "E189.22.5", {"start": v(27.1, 24) * mm, "mid": v(28.46, 23.1) * mm, "end": v(30.1, 22.99) * mm});
            skArc(sketch, "E189.23.0", {"start": v(26.45, 27.11) * mm, "mid": v(26.36, 25.47) * mm, "end": v(27.1, 24) * mm});
            skLineSegment(sketch, "E189.23.1", {"start": v(27.46, 30.24) * mm, "end": v(26.45, 27.11) * mm});
            skArc(sketch, "E189.23.2", {"start": v(27.46, 30.24) * mm, "mid": v(27.28, 30.41) * mm, "end": v(27.09, 30.58) * mm});
            skArc(sketch, "E189.23.3", {"start": v(27.09, 30.58) * mm, "mid": v(26.9, 30.74) * mm, "end": v(26.71, 30.9) * mm});
            skLineSegment(sketch, "E189.23.4", {"start": v(26.71, 30.9) * mm, "end": v(23.73, 29.52) * mm});
            skArc(sketch, "E189.23.5", {"start": v(20.56, 29.8) * mm, "mid": v(22.1, 29.24) * mm, "end": v(23.73, 29.52) * mm});
            skArc(sketch, "E189.24.0", {"start": v(19.19, 32.65) * mm, "mid": v(19.5, 31.04) * mm, "end": v(20.56, 29.8) * mm});
            skLineSegment(sketch, "E189.24.1", {"start": v(19.43, 35.94) * mm, "end": v(19.19, 32.65) * mm});
            skArc(sketch, "E189.24.2", {"start": v(19.43, 35.94) * mm, "mid": v(19.2, 36.05) * mm, "end": v(18.98, 36.17) * mm});
            skArc(sketch, "E189.24.3", {"start": v(18.98, 36.17) * mm, "mid": v(18.76, 36.29) * mm, "end": v(18.54, 36.4) * mm});
            skLineSegment(sketch, "E189.24.4", {"start": v(18.54, 36.4) * mm, "end": v(15.97, 34.34) * mm});
            skArc(sketch, "E189.24.5", {"start": v(12.84, 33.85) * mm, "mid": v(14.47, 33.68) * mm, "end": v(15.97, 34.34) * mm});
            skArc(sketch, "E189.25.0", {"start": v(10.82, 36.3) * mm, "mid": v(11.5, 34.8) * mm, "end": v(12.84, 33.85) * mm});
            skLineSegment(sketch, "E189.25.1", {"start": v(10.26, 39.54) * mm, "end": v(10.82, 36.3) * mm});
            skArc(sketch, "E189.25.2", {"start": v(10.26, 39.54) * mm, "mid": v(10.02, 39.6) * mm, "end": v(9.78, 39.66) * mm});
            skArc(sketch, "E189.25.3", {"start": v(9.78, 39.66) * mm, "mid": v(9.53, 39.72) * mm, "end": v(9.29, 39.78) * mm});
            skLineSegment(sketch, "E189.25.4", {"start": v(9.29, 39.78) * mm, "end": v(7.3, 37.17) * mm});
            skArc(sketch, "E189.25.5", {"start": v(4.36, 35.94) * mm, "mid": v(6, 36.16) * mm, "end": v(7.3, 37.17) * mm});
            skCircle(sketch, "E190", {"center": v(0, 0) * mm, "radius": 41.97 * mm});
            skSolve(sketch);
        }
        {
            var Q0;
            Q0=makeQuery(id+"F6.imprint","IMPRINT",FACE,{"disambiguationData":[TD([[makeQuery(id+"F6.imprint","IMPRINT",EDGE,{"derivedFrom":sQuery(id+"F6.wireOp",EDGE,"E183")}),-1.0]])]});
            extrude(context, id + "F7", {"entities" : qUnion([Q0]), "operationType" : NewBodyOperationType.REMOVE, "oppositeDirection" : true, "depth" : 6 * mm, "offsetDistance" : 25 * mm});
        }
        {
            var Q0;
            Q0=makeQuery(id+"F1.opRevolve","SWEPT_FACE",FACE,{"disambiguationData":[OSD([sQuery(id+"F0.wireOp",EDGE,"E32")])]});
            var sketch = newSketch(context, id + "F8", { "sketchPlane" : qUnion([Q0])});
            skArc(sketch, "E191", {"start": v(1.43, 36.17) * mm, "mid": v(2.2, 36.23) * mm, "end": v(2.93, 36.48) * mm});
            skArc(sketch, "E192", {"start": v(7.01, 40.24) * mm, "mid": v(6.76, 40.29) * mm, "end": v(6.52, 40.33) * mm});
            skArc(sketch, "E193", {"start": v(7.83, 37.06) * mm, "mid": v(8.63, 35.63) * mm, "end": v(10.04, 34.78) * mm});
            skArc(sketch, "E194", {"start": v(6.52, 40.33) * mm, "mid": v(6.27, 40.37) * mm, "end": v(6.02, 40.4) * mm});
            skArc(sketch, "E195", {"start": v(2.93, 36.48) * mm, "mid": v(3.67, 36.97) * mm, "end": v(4.24, 37.64) * mm});
            skLineSegment(sketch, "E196", {"start": v(6.02, 40.4) * mm, "end": v(4.24, 37.64) * mm});
            skLineSegment(sketch, "E197", {"start": v(7.67, 37.67) * mm, "end": v(7.83, 37.06) * mm});
            skLineSegment(sketch, "E198", {"start": v(7.01, 40.24) * mm, "end": v(7.67, 37.67) * mm});
            skArc(sketch, "E199.1.0", {"start": v(-7.27, 35.46) * mm, "mid": v(-6.54, 35.7) * mm, "end": v(-5.89, 36.12) * mm});
            skArc(sketch, "E199.1.1", {"start": v(-5.89, 36.12) * mm, "mid": v(-5.29, 36.77) * mm, "end": v(-4.89, 37.56) * mm});
            skLineSegment(sketch, "E199.1.2", {"start": v(-3.82, 40.67) * mm, "end": v(-4.89, 37.56) * mm});
            skArc(sketch, "E199.1.3", {"start": v(-3.32, 40.71) * mm, "mid": v(-3.57, 40.7) * mm, "end": v(-3.82, 40.67) * mm});
            skArc(sketch, "E199.1.4", {"start": v(-2.82, 40.75) * mm, "mid": v(-3.07, 40.73) * mm, "end": v(-3.32, 40.71) * mm});
            skLineSegment(sketch, "E199.1.5", {"start": v(-2.82, 40.75) * mm, "end": v(-1.56, 38.4) * mm});
            skLineSegment(sketch, "E199.1.6", {"start": v(-1.56, 38.4) * mm, "end": v(-1.27, 37.85) * mm});
            skArc(sketch, "E199.1.7", {"start": v(-1.27, 37.85) * mm, "mid": v(-0.14, 36.66) * mm, "end": v(1.43, 36.17) * mm});
            skArc(sketch, "E199.2.0", {"start": v(-15.55, 32.7) * mm, "mid": v(-14.9, 33.1) * mm, "end": v(-14.36, 33.66) * mm});
            skArc(sketch, "E199.2.1", {"start": v(-14.36, 33.66) * mm, "mid": v(-13.93, 34.44) * mm, "end": v(-13.73, 35.3) * mm});
            skLineSegment(sketch, "E199.2.2", {"start": v(-13.44, 38.57) * mm, "end": v(-13.73, 35.3) * mm});
            skArc(sketch, "E199.2.3", {"start": v(-12.97, 38.74) * mm, "mid": v(-13.2, 38.66) * mm, "end": v(-13.44, 38.57) * mm});
            skArc(sketch, "E199.2.4", {"start": v(-12.5, 38.9) * mm, "mid": v(-12.73, 38.81) * mm, "end": v(-12.97, 38.74) * mm});
            skLineSegment(sketch, "E199.2.5", {"start": v(-12.5, 38.9) * mm, "end": v(-10.71, 36.92) * mm});
            skLineSegment(sketch, "E199.2.6", {"start": v(-10.71, 36.92) * mm, "end": v(-10.29, 36.45) * mm});
            skArc(sketch, "E199.2.7", {"start": v(-10.29, 36.45) * mm, "mid": v(-8.91, 35.56) * mm, "end": v(-7.27, 35.46) * mm});
            skArc(sketch, "E199.3.0", {"start": v(-22.92, 28.02) * mm, "mid": v(-22.38, 28.58) * mm, "end": v(-22, 29.25) * mm});
            skArc(sketch, "E199.3.1", {"start": v(-22, 29.25) * mm, "mid": v(-21.77, 30.1) * mm, "end": v(-21.78, 30.99) * mm});
            skLineSegment(sketch, "E199.3.2", {"start": v(-22.28, 34.24) * mm, "end": v(-21.78, 30.99) * mm});
            skArc(sketch, "E199.3.3", {"start": v(-21.86, 34.5) * mm, "mid": v(-22.07, 34.37) * mm, "end": v(-22.28, 34.24) * mm});
            skArc(sketch, "E199.3.4", {"start": v(-21.44, 34.77) * mm, "mid": v(-21.65, 34.64) * mm, "end": v(-21.86, 34.5) * mm});
            skLineSegment(sketch, "E199.3.5", {"start": v(-21.44, 34.77) * mm, "end": v(-19.23, 33.28) * mm});
            skLineSegment(sketch, "E199.3.6", {"start": v(-19.23, 33.28) * mm, "end": v(-18.71, 32.93) * mm});
            skArc(sketch, "E199.3.7", {"start": v(-18.71, 32.93) * mm, "mid": v(-17.16, 32.4) * mm, "end": v(-15.55, 32.7) * mm});
            skArc(sketch, "E199.4.0", {"start": v(-28.96, 21.72) * mm, "mid": v(-28.57, 22.4) * mm, "end": v(-28.36, 23.13) * mm});
            skArc(sketch, "E199.4.1", {"start": v(-28.36, 23.13) * mm, "mid": v(-28.34, 24.02) * mm, "end": v(-28.56, 24.87) * mm});
            skLineSegment(sketch, "E199.4.2", {"start": v(-29.83, 27.9) * mm, "end": v(-28.56, 24.87) * mm});
            skArc(sketch, "E199.4.3", {"start": v(-29.49, 28.27) * mm, "mid": v(-29.66, 28.1) * mm, "end": v(-29.83, 27.9) * mm});
            skArc(sketch, "E199.4.4", {"start": v(-29.14, 28.63) * mm, "mid": v(-29.31, 28.45) * mm, "end": v(-29.49, 28.27) * mm});
            skLineSegment(sketch, "E199.4.5", {"start": v(-29.14, 28.63) * mm, "end": v(-26.64, 27.71) * mm});
            skLineSegment(sketch, "E199.4.6", {"start": v(-26.64, 27.71) * mm, "end": v(-26.05, 27.5) * mm});
            skArc(sketch, "E199.4.7", {"start": v(-26.05, 27.5) * mm, "mid": v(-24.42, 27.34) * mm, "end": v(-22.92, 28.02) * mm});
            skArc(sketch, "E199.5.0", {"start": v(-33.32, 14.16) * mm, "mid": v(-33.1, 14.9) * mm, "end": v(-33.07, 15.67) * mm});
            skArc(sketch, "E199.5.1", {"start": v(-33.07, 15.67) * mm, "mid": v(-33.27, 16.54) * mm, "end": v(-33.69, 17.31) * mm});
            skLineSegment(sketch, "E199.5.2", {"start": v(-35.64, 19.96) * mm, "end": v(-33.69, 17.31) * mm});
            skArc(sketch, "E199.5.3", {"start": v(-35.4, 20.4) * mm, "mid": v(-35.52, 20.18) * mm, "end": v(-35.64, 19.96) * mm});
            skArc(sketch, "E199.5.4", {"start": v(-35.14, 20.83) * mm, "mid": v(-35.27, 20.6) * mm, "end": v(-35.4, 20.4) * mm});
            skLineSegment(sketch, "E199.5.5", {"start": v(-35.14, 20.83) * mm, "end": v(-32.5, 20.53) * mm});
            skLineSegment(sketch, "E199.5.6", {"start": v(-32.5, 20.53) * mm, "end": v(-31.87, 20.46) * mm});
            skArc(sketch, "E199.5.7", {"start": v(-31.87, 20.46) * mm, "mid": v(-30.25, 20.7) * mm, "end": v(-28.96, 21.72) * mm});
            skArc(sketch, "E199.6.0", {"start": v(-35.74, 5.78) * mm, "mid": v(-35.7, 6.55) * mm, "end": v(-35.86, 7.3) * mm});
            skArc(sketch, "E199.6.1", {"start": v(-35.86, 7.3) * mm, "mid": v(-36.26, 8.1) * mm, "end": v(-36.85, 8.75) * mm});
            skLineSegment(sketch, "E199.6.2", {"start": v(-39.38, 10.85) * mm, "end": v(-36.85, 8.75) * mm});
            skArc(sketch, "E199.6.3", {"start": v(-39.25, 11.33) * mm, "mid": v(-39.32, 11.1) * mm, "end": v(-39.38, 10.85) * mm});
            skArc(sketch, "E199.6.4", {"start": v(-39.1, 11.81) * mm, "mid": v(-39.18, 11.57) * mm, "end": v(-39.25, 11.33) * mm});
            skLineSegment(sketch, "E199.6.5", {"start": v(-39.1, 11.81) * mm, "end": v(-36.47, 12.16) * mm});
            skLineSegment(sketch, "E199.6.6", {"start": v(-36.47, 12.16) * mm, "end": v(-35.84, 12.24) * mm});
            skArc(sketch, "E199.6.7", {"start": v(-35.84, 12.24) * mm, "mid": v(-34.32, 12.86) * mm, "end": v(-33.32, 14.16) * mm});
            skArc(sketch, "E199.7.0", {"start": v(-36.08, -2.94) * mm, "mid": v(-36.24, -2.19) * mm, "end": v(-36.57, -1.49) * mm});
            skArc(sketch, "E199.7.1", {"start": v(-36.57, -1.49) * mm, "mid": v(-37.14, -0.82) * mm, "end": v(-37.87, -0.33) * mm});
            skLineSegment(sketch, "E199.7.2", {"start": v(-40.83, 1.1) * mm, "end": v(-37.87, -0.33) * mm});
            skArc(sketch, "E199.7.3", {"start": v(-40.82, 1.6) * mm, "mid": v(-40.83, 1.36) * mm, "end": v(-40.83, 1.1) * mm});
            skArc(sketch, "E199.7.4", {"start": v(-40.8, 2.1) * mm, "mid": v(-40.8, 1.86) * mm, "end": v(-40.82, 1.6) * mm});
            skLineSegment(sketch, "E199.7.5", {"start": v(-40.8, 2.1) * mm, "end": v(-38.32, 3.08) * mm});
            skLineSegment(sketch, "E199.7.6", {"start": v(-38.32, 3.08) * mm, "end": v(-37.73, 3.3) * mm});
            skArc(sketch, "E199.7.7", {"start": v(-37.73, 3.3) * mm, "mid": v(-36.4, 4.28) * mm, "end": v(-35.74, 5.78) * mm});
            skArc(sketch, "E199.8.0", {"start": v(-34.33, -11.5) * mm, "mid": v(-34.66, -10.8) * mm, "end": v(-35.15, -10.2) * mm});
            skArc(sketch, "E199.8.1", {"start": v(-35.15, -10.2) * mm, "mid": v(-35.87, -9.68) * mm, "end": v(-36.7, -9.38) * mm});
            skLineSegment(sketch, "E199.8.2", {"start": v(-39.91, -8.7) * mm, "end": v(-36.7, -9.38) * mm});
            skArc(sketch, "E199.8.3", {"start": v(-40.02, -8.2) * mm, "mid": v(-39.97, -8.45) * mm, "end": v(-39.91, -8.7) * mm});
            skArc(sketch, "E199.8.4", {"start": v(-40.11, -7.72) * mm, "mid": v(-40.07, -7.96) * mm, "end": v(-40.02, -8.2) * mm});
            skLineSegment(sketch, "E199.8.5", {"start": v(-40.11, -7.72) * mm, "end": v(-37.94, -6.18) * mm});
            skLineSegment(sketch, "E199.8.6", {"start": v(-37.94, -6.18) * mm, "end": v(-37.43, -5.82) * mm});
            skArc(sketch, "E199.8.7", {"start": v(-37.43, -5.82) * mm, "mid": v(-36.37, -4.56) * mm, "end": v(-36.08, -2.94) * mm});
            skArc(sketch, "E199.9.0", {"start": v(-30.58, -19.37) * mm, "mid": v(-31.07, -18.78) * mm, "end": v(-31.69, -18.31) * mm});
            skArc(sketch, "E199.9.1", {"start": v(-31.69, -18.31) * mm, "mid": v(-32.5, -17.98) * mm, "end": v(-33.38, -17.89) * mm});
            skLineSegment(sketch, "E199.9.2", {"start": v(-36.67, -18) * mm, "end": v(-33.38, -17.89) * mm});
            skArc(sketch, "E199.9.3", {"start": v(-36.9, -17.54) * mm, "mid": v(-36.78, -17.77) * mm, "end": v(-36.67, -18) * mm});
            skArc(sketch, "E199.9.4", {"start": v(-37.1, -17.1) * mm, "mid": v(-37, -17.32) * mm, "end": v(-36.9, -17.54) * mm});
            skLineSegment(sketch, "E199.9.5", {"start": v(-37.1, -17.1) * mm, "end": v(-35.36, -15.08) * mm});
            skLineSegment(sketch, "E199.9.6", {"start": v(-35.36, -15.08) * mm, "end": v(-34.95, -14.6) * mm});
            skArc(sketch, "E199.9.7", {"start": v(-34.95, -14.6) * mm, "mid": v(-34.22, -13.13) * mm, "end": v(-34.33, -11.5) * mm});
            skArc(sketch, "E199.10.0", {"start": v(-25.05, -26.13) * mm, "mid": v(-25.67, -25.67) * mm, "end": v(-26.38, -25.36) * mm});
            skArc(sketch, "E199.10.1", {"start": v(-26.38, -25.36) * mm, "mid": v(-27.26, -25.24) * mm, "end": v(-28.13, -25.36) * mm});
            skLineSegment(sketch, "E199.10.2", {"start": v(-31.3, -26.25) * mm, "end": v(-28.13, -25.36) * mm});
            skArc(sketch, "E199.10.3", {"start": v(-31.62, -25.86) * mm, "mid": v(-31.46, -26.06) * mm, "end": v(-31.3, -26.25) * mm});
            skArc(sketch, "E199.10.4", {"start": v(-31.93, -25.47) * mm, "mid": v(-31.78, -25.67) * mm, "end": v(-31.62, -25.86) * mm});
            skLineSegment(sketch, "E199.10.5", {"start": v(-31.93, -25.47) * mm, "end": v(-30.72, -23.1) * mm});
            skLineSegment(sketch, "E199.10.6", {"start": v(-30.72, -23.1) * mm, "end": v(-30.43, -22.55) * mm});
            skArc(sketch, "E199.10.7", {"start": v(-30.43, -22.55) * mm, "mid": v(-30.09, -20.94) * mm, "end": v(-30.58, -19.37) * mm});
            skArc(sketch, "E199.11.0", {"start": v(-18.07, -31.37) * mm, "mid": v(-18.78, -31.06) * mm, "end": v(-19.55, -30.94) * mm});
            skArc(sketch, "E199.11.1", {"start": v(-19.55, -30.94) * mm, "mid": v(-20.43, -31.03) * mm, "end": v(-21.25, -31.35) * mm});
            skLineSegment(sketch, "E199.11.2", {"start": v(-24.1, -32.98) * mm, "end": v(-21.25, -31.35) * mm});
            skArc(sketch, "E199.11.3", {"start": v(-24.51, -32.68) * mm, "mid": v(-24.31, -32.83) * mm, "end": v(-24.1, -32.98) * mm});
            skArc(sketch, "E199.11.4", {"start": v(-24.9, -32.38) * mm, "mid": v(-24.71, -32.53) * mm, "end": v(-24.51, -32.68) * mm});
            skLineSegment(sketch, "E199.11.5", {"start": v(-24.9, -32.38) * mm, "end": v(-24.3, -29.79) * mm});
            skLineSegment(sketch, "E199.11.6", {"start": v(-24.3, -29.79) * mm, "end": v(-24.15, -29.17) * mm});
            skArc(sketch, "E199.11.7", {"start": v(-24.15, -29.17) * mm, "mid": v(-24.2, -27.53) * mm, "end": v(-25.05, -26.13) * mm});
            skArc(sketch, "E199.12.0", {"start": v(-10.04, -34.78) * mm, "mid": v(-10.8, -34.66) * mm, "end": v(-11.57, -34.72) * mm});
            skArc(sketch, "E199.12.1", {"start": v(-11.57, -34.72) * mm, "mid": v(-12.4, -35.02) * mm, "end": v(-13.13, -35.53) * mm});
            skLineSegment(sketch, "E199.12.2", {"start": v(-15.52, -37.79) * mm, "end": v(-13.13, -35.53) * mm});
            skArc(sketch, "E199.12.3", {"start": v(-15.98, -37.6) * mm, "mid": v(-15.75, -37.7) * mm, "end": v(-15.52, -37.79) * mm});
            skArc(sketch, "E199.12.4", {"start": v(-16.44, -37.4) * mm, "mid": v(-16.2, -37.5) * mm, "end": v(-15.98, -37.6) * mm});
            skLineSegment(sketch, "E199.12.5", {"start": v(-16.44, -37.4) * mm, "end": v(-16.46, -34.74) * mm});
            skLineSegment(sketch, "E199.12.6", {"start": v(-16.46, -34.74) * mm, "end": v(-16.47, -34.1) * mm});
            skArc(sketch, "E199.12.7", {"start": v(-16.47, -34.1) * mm, "mid": v(-16.9, -32.52) * mm, "end": v(-18.07, -31.37) * mm});
            skArc(sketch, "E199.13.0", {"start": v(-1.43, -36.17) * mm, "mid": v(-2.2, -36.23) * mm, "end": v(-2.93, -36.48) * mm});
            skArc(sketch, "E199.13.1", {"start": v(-2.93, -36.48) * mm, "mid": v(-3.67, -36.97) * mm, "end": v(-4.24, -37.64) * mm});
            skLineSegment(sketch, "E199.13.2", {"start": v(-6.02, -40.4) * mm, "end": v(-4.24, -37.64) * mm});
            skArc(sketch, "E199.13.3", {"start": v(-6.52, -40.33) * mm, "mid": v(-6.27, -40.37) * mm, "end": v(-6.02, -40.4) * mm});
            skArc(sketch, "E199.13.4", {"start": v(-7.01, -40.24) * mm, "mid": v(-6.76, -40.29) * mm, "end": v(-6.52, -40.33) * mm});
            skLineSegment(sketch, "E199.13.5", {"start": v(-7.01, -40.24) * mm, "end": v(-7.67, -37.67) * mm});
            skLineSegment(sketch, "E199.13.6", {"start": v(-7.67, -37.67) * mm, "end": v(-7.83, -37.06) * mm});
            skArc(sketch, "E199.13.7", {"start": v(-7.83, -37.06) * mm, "mid": v(-8.63, -35.63) * mm, "end": v(-10.04, -34.78) * mm});
            skArc(sketch, "E199.14.0", {"start": v(7.27, -35.46) * mm, "mid": v(6.54, -35.7) * mm, "end": v(5.89, -36.12) * mm});
            skArc(sketch, "E199.14.1", {"start": v(5.89, -36.12) * mm, "mid": v(5.29, -36.77) * mm, "end": v(4.89, -37.56) * mm});
            skLineSegment(sketch, "E199.14.2", {"start": v(3.82, -40.67) * mm, "end": v(4.89, -37.56) * mm});
            skArc(sketch, "E199.14.3", {"start": v(3.32, -40.71) * mm, "mid": v(3.57, -40.7) * mm, "end": v(3.82, -40.67) * mm});
            skArc(sketch, "E199.14.4", {"start": v(2.82, -40.75) * mm, "mid": v(3.07, -40.73) * mm, "end": v(3.32, -40.71) * mm});
            skLineSegment(sketch, "E199.14.5", {"start": v(2.82, -40.75) * mm, "end": v(1.56, -38.4) * mm});
            skLineSegment(sketch, "E199.14.6", {"start": v(1.56, -38.4) * mm, "end": v(1.27, -37.85) * mm});
            skArc(sketch, "E199.14.7", {"start": v(1.27, -37.85) * mm, "mid": v(0.14, -36.66) * mm, "end": v(-1.43, -36.17) * mm});
            skArc(sketch, "E199.15.0", {"start": v(15.55, -32.7) * mm, "mid": v(14.9, -33.1) * mm, "end": v(14.36, -33.66) * mm});
            skArc(sketch, "E199.15.1", {"start": v(14.36, -33.66) * mm, "mid": v(13.93, -34.44) * mm, "end": v(13.73, -35.3) * mm});
            skLineSegment(sketch, "E199.15.2", {"start": v(13.44, -38.57) * mm, "end": v(13.73, -35.3) * mm});
            skArc(sketch, "E199.15.3", {"start": v(12.97, -38.74) * mm, "mid": v(13.2, -38.66) * mm, "end": v(13.44, -38.57) * mm});
            skArc(sketch, "E199.15.4", {"start": v(12.5, -38.9) * mm, "mid": v(12.73, -38.81) * mm, "end": v(12.97, -38.74) * mm});
            skLineSegment(sketch, "E199.15.5", {"start": v(12.5, -38.9) * mm, "end": v(10.71, -36.92) * mm});
            skLineSegment(sketch, "E199.15.6", {"start": v(10.71, -36.92) * mm, "end": v(10.29, -36.45) * mm});
            skArc(sketch, "E199.15.7", {"start": v(10.29, -36.45) * mm, "mid": v(8.91, -35.56) * mm, "end": v(7.27, -35.46) * mm});
            skArc(sketch, "E199.16.0", {"start": v(22.92, -28.02) * mm, "mid": v(22.38, -28.58) * mm, "end": v(22, -29.25) * mm});
            skArc(sketch, "E199.16.1", {"start": v(22, -29.25) * mm, "mid": v(21.77, -30.1) * mm, "end": v(21.78, -30.99) * mm});
            skLineSegment(sketch, "E199.16.2", {"start": v(22.28, -34.24) * mm, "end": v(21.78, -30.99) * mm});
            skArc(sketch, "E199.16.3", {"start": v(21.86, -34.5) * mm, "mid": v(22.07, -34.37) * mm, "end": v(22.28, -34.24) * mm});
            skArc(sketch, "E199.16.4", {"start": v(21.44, -34.77) * mm, "mid": v(21.65, -34.64) * mm, "end": v(21.86, -34.5) * mm});
            skLineSegment(sketch, "E199.16.5", {"start": v(21.44, -34.77) * mm, "end": v(19.23, -33.28) * mm});
            skLineSegment(sketch, "E199.16.6", {"start": v(19.23, -33.28) * mm, "end": v(18.71, -32.93) * mm});
            skArc(sketch, "E199.16.7", {"start": v(18.71, -32.93) * mm, "mid": v(17.16, -32.4) * mm, "end": v(15.55, -32.7) * mm});
            skArc(sketch, "E199.17.0", {"start": v(28.96, -21.72) * mm, "mid": v(28.57, -22.4) * mm, "end": v(28.36, -23.13) * mm});
            skArc(sketch, "E199.17.1", {"start": v(28.36, -23.13) * mm, "mid": v(28.34, -24.02) * mm, "end": v(28.56, -24.87) * mm});
            skLineSegment(sketch, "E199.17.2", {"start": v(29.83, -27.9) * mm, "end": v(28.56, -24.87) * mm});
            skArc(sketch, "E199.17.3", {"start": v(29.49, -28.27) * mm, "mid": v(29.66, -28.1) * mm, "end": v(29.83, -27.9) * mm});
            skArc(sketch, "E199.17.4", {"start": v(29.14, -28.63) * mm, "mid": v(29.31, -28.45) * mm, "end": v(29.49, -28.27) * mm});
            skLineSegment(sketch, "E199.17.5", {"start": v(29.14, -28.63) * mm, "end": v(26.64, -27.71) * mm});
            skLineSegment(sketch, "E199.17.6", {"start": v(26.64, -27.71) * mm, "end": v(26.05, -27.5) * mm});
            skArc(sketch, "E199.17.7", {"start": v(26.05, -27.5) * mm, "mid": v(24.42, -27.34) * mm, "end": v(22.92, -28.02) * mm});
            skArc(sketch, "E199.18.0", {"start": v(33.32, -14.16) * mm, "mid": v(33.1, -14.9) * mm, "end": v(33.07, -15.67) * mm});
            skArc(sketch, "E199.18.1", {"start": v(33.07, -15.67) * mm, "mid": v(33.27, -16.54) * mm, "end": v(33.69, -17.31) * mm});
            skLineSegment(sketch, "E199.18.2", {"start": v(35.64, -19.96) * mm, "end": v(33.69, -17.31) * mm});
            skArc(sketch, "E199.18.3", {"start": v(35.4, -20.4) * mm, "mid": v(35.52, -20.18) * mm, "end": v(35.64, -19.96) * mm});
            skArc(sketch, "E199.18.4", {"start": v(35.14, -20.83) * mm, "mid": v(35.27, -20.6) * mm, "end": v(35.4, -20.4) * mm});
            skLineSegment(sketch, "E199.18.5", {"start": v(35.14, -20.83) * mm, "end": v(32.5, -20.53) * mm});
            skLineSegment(sketch, "E199.18.6", {"start": v(32.5, -20.53) * mm, "end": v(31.87, -20.46) * mm});
            skArc(sketch, "E199.18.7", {"start": v(31.87, -20.46) * mm, "mid": v(30.25, -20.7) * mm, "end": v(28.96, -21.72) * mm});
            skArc(sketch, "E199.19.0", {"start": v(35.74, -5.78) * mm, "mid": v(35.7, -6.55) * mm, "end": v(35.86, -7.3) * mm});
            skArc(sketch, "E199.19.1", {"start": v(35.86, -7.3) * mm, "mid": v(36.26, -8.1) * mm, "end": v(36.85, -8.75) * mm});
            skLineSegment(sketch, "E199.19.2", {"start": v(39.38, -10.85) * mm, "end": v(36.85, -8.75) * mm});
            skArc(sketch, "E199.19.3", {"start": v(39.25, -11.33) * mm, "mid": v(39.32, -11.1) * mm, "end": v(39.38, -10.85) * mm});
            skArc(sketch, "E199.19.4", {"start": v(39.1, -11.81) * mm, "mid": v(39.18, -11.57) * mm, "end": v(39.25, -11.33) * mm});
            skLineSegment(sketch, "E199.19.5", {"start": v(39.1, -11.81) * mm, "end": v(36.47, -12.16) * mm});
            skLineSegment(sketch, "E199.19.6", {"start": v(36.47, -12.16) * mm, "end": v(35.84, -12.24) * mm});
            skArc(sketch, "E199.19.7", {"start": v(35.84, -12.24) * mm, "mid": v(34.32, -12.86) * mm, "end": v(33.32, -14.16) * mm});
            skArc(sketch, "E199.20.0", {"start": v(36.08, 2.94) * mm, "mid": v(36.24, 2.19) * mm, "end": v(36.57, 1.49) * mm});
            skArc(sketch, "E199.20.1", {"start": v(36.57, 1.49) * mm, "mid": v(37.14, 0.82) * mm, "end": v(37.87, 0.33) * mm});
            skLineSegment(sketch, "E199.20.2", {"start": v(40.83, -1.1) * mm, "end": v(37.87, 0.33) * mm});
            skArc(sketch, "E199.20.3", {"start": v(40.82, -1.6) * mm, "mid": v(40.83, -1.36) * mm, "end": v(40.83, -1.1) * mm});
            skArc(sketch, "E199.20.4", {"start": v(40.8, -2.1) * mm, "mid": v(40.8, -1.86) * mm, "end": v(40.82, -1.6) * mm});
            skLineSegment(sketch, "E199.20.5", {"start": v(40.8, -2.1) * mm, "end": v(38.32, -3.08) * mm});
            skLineSegment(sketch, "E199.20.6", {"start": v(38.32, -3.08) * mm, "end": v(37.73, -3.3) * mm});
            skArc(sketch, "E199.20.7", {"start": v(37.73, -3.3) * mm, "mid": v(36.4, -4.28) * mm, "end": v(35.74, -5.78) * mm});
            skArc(sketch, "E199.21.0", {"start": v(34.33, 11.5) * mm, "mid": v(34.66, 10.8) * mm, "end": v(35.15, 10.2) * mm});
            skArc(sketch, "E199.21.1", {"start": v(35.15, 10.2) * mm, "mid": v(35.87, 9.68) * mm, "end": v(36.7, 9.38) * mm});
            skLineSegment(sketch, "E199.21.2", {"start": v(39.91, 8.7) * mm, "end": v(36.7, 9.38) * mm});
            skArc(sketch, "E199.21.3", {"start": v(40.02, 8.2) * mm, "mid": v(39.97, 8.45) * mm, "end": v(39.91, 8.7) * mm});
            skArc(sketch, "E199.21.4", {"start": v(40.11, 7.72) * mm, "mid": v(40.07, 7.96) * mm, "end": v(40.02, 8.2) * mm});
            skLineSegment(sketch, "E199.21.5", {"start": v(40.11, 7.72) * mm, "end": v(37.94, 6.18) * mm});
            skLineSegment(sketch, "E199.21.6", {"start": v(37.94, 6.18) * mm, "end": v(37.43, 5.82) * mm});
            skArc(sketch, "E199.21.7", {"start": v(37.43, 5.82) * mm, "mid": v(36.37, 4.56) * mm, "end": v(36.08, 2.94) * mm});
            skArc(sketch, "E199.22.0", {"start": v(30.58, 19.37) * mm, "mid": v(31.07, 18.78) * mm, "end": v(31.69, 18.31) * mm});
            skArc(sketch, "E199.22.1", {"start": v(31.69, 18.31) * mm, "mid": v(32.5, 17.98) * mm, "end": v(33.38, 17.89) * mm});
            skLineSegment(sketch, "E199.22.2", {"start": v(36.67, 18) * mm, "end": v(33.38, 17.89) * mm});
            skArc(sketch, "E199.22.3", {"start": v(36.9, 17.54) * mm, "mid": v(36.78, 17.77) * mm, "end": v(36.67, 18) * mm});
            skArc(sketch, "E199.22.4", {"start": v(37.1, 17.1) * mm, "mid": v(37, 17.32) * mm, "end": v(36.9, 17.54) * mm});
            skLineSegment(sketch, "E199.22.5", {"start": v(37.1, 17.1) * mm, "end": v(35.36, 15.08) * mm});
            skLineSegment(sketch, "E199.22.6", {"start": v(35.36, 15.08) * mm, "end": v(34.95, 14.6) * mm});
            skArc(sketch, "E199.22.7", {"start": v(34.95, 14.6) * mm, "mid": v(34.22, 13.13) * mm, "end": v(34.33, 11.5) * mm});
            skArc(sketch, "E199.23.0", {"start": v(25.05, 26.13) * mm, "mid": v(25.67, 25.67) * mm, "end": v(26.38, 25.36) * mm});
            skArc(sketch, "E199.23.1", {"start": v(26.38, 25.36) * mm, "mid": v(27.26, 25.24) * mm, "end": v(28.13, 25.36) * mm});
            skLineSegment(sketch, "E199.23.2", {"start": v(31.3, 26.25) * mm, "end": v(28.13, 25.36) * mm});
            skArc(sketch, "E199.23.3", {"start": v(31.62, 25.86) * mm, "mid": v(31.46, 26.06) * mm, "end": v(31.3, 26.25) * mm});
            skArc(sketch, "E199.23.4", {"start": v(31.93, 25.47) * mm, "mid": v(31.78, 25.67) * mm, "end": v(31.62, 25.86) * mm});
            skLineSegment(sketch, "E199.23.5", {"start": v(31.93, 25.47) * mm, "end": v(30.72, 23.1) * mm});
            skLineSegment(sketch, "E199.23.6", {"start": v(30.72, 23.1) * mm, "end": v(30.43, 22.55) * mm});
            skArc(sketch, "E199.23.7", {"start": v(30.43, 22.55) * mm, "mid": v(30.09, 20.94) * mm, "end": v(30.58, 19.37) * mm});
            skArc(sketch, "E199.24.0", {"start": v(18.07, 31.37) * mm, "mid": v(18.78, 31.06) * mm, "end": v(19.55, 30.94) * mm});
            skArc(sketch, "E199.24.1", {"start": v(19.55, 30.94) * mm, "mid": v(20.43, 31.03) * mm, "end": v(21.25, 31.35) * mm});
            skLineSegment(sketch, "E199.24.2", {"start": v(24.1, 32.98) * mm, "end": v(21.25, 31.35) * mm});
            skArc(sketch, "E199.24.3", {"start": v(24.51, 32.68) * mm, "mid": v(24.31, 32.83) * mm, "end": v(24.1, 32.98) * mm});
            skArc(sketch, "E199.24.4", {"start": v(24.9, 32.38) * mm, "mid": v(24.71, 32.53) * mm, "end": v(24.51, 32.68) * mm});
            skLineSegment(sketch, "E199.24.5", {"start": v(24.9, 32.38) * mm, "end": v(24.3, 29.79) * mm});
            skLineSegment(sketch, "E199.24.6", {"start": v(24.3, 29.79) * mm, "end": v(24.15, 29.17) * mm});
            skArc(sketch, "E199.24.7", {"start": v(24.15, 29.17) * mm, "mid": v(24.2, 27.53) * mm, "end": v(25.05, 26.13) * mm});
            skArc(sketch, "E199.25.0", {"start": v(10.04, 34.78) * mm, "mid": v(10.8, 34.66) * mm, "end": v(11.57, 34.72) * mm});
            skArc(sketch, "E199.25.1", {"start": v(11.57, 34.72) * mm, "mid": v(12.4, 35.02) * mm, "end": v(13.13, 35.53) * mm});
            skLineSegment(sketch, "E199.25.2", {"start": v(15.52, 37.79) * mm, "end": v(13.13, 35.53) * mm});
            skArc(sketch, "E199.25.3", {"start": v(15.98, 37.6) * mm, "mid": v(15.75, 37.7) * mm, "end": v(15.52, 37.79) * mm});
            skArc(sketch, "E199.25.4", {"start": v(16.44, 37.4) * mm, "mid": v(16.2, 37.5) * mm, "end": v(15.98, 37.6) * mm});
            skLineSegment(sketch, "E199.25.5", {"start": v(16.44, 37.4) * mm, "end": v(16.46, 34.74) * mm});
            skLineSegment(sketch, "E199.25.6", {"start": v(16.46, 34.74) * mm, "end": v(16.47, 34.1) * mm});
            skArc(sketch, "E199.25.7", {"start": v(16.47, 34.1) * mm, "mid": v(16.9, 32.52) * mm, "end": v(18.07, 31.37) * mm});
            skCircle(sketch, "E200", {"center": v(0, 0) * mm, "radius": 43.06 * mm});
            skSolve(sketch);
        }
        {
            var Q0;
            Q0=makeQuery(id+"F8.imprint","IMPRINT",FACE,{"disambiguationData":[TD([[makeQuery(id+"F8.imprint","IMPRINT",EDGE,{"derivedFrom":sQuery(id+"F8.wireOp",EDGE,"E191")}),1.0]])]});
            extrude(context, id + "F9", {"entities" : qUnion([Q0]), "operationType" : NewBodyOperationType.REMOVE, "oppositeDirection" : true, "depth" : 6 * mm, "offsetDistance" : 25 * mm});
        }
        {
            var Q0;
            Q0=makeQuery(id+"F1.opRevolve","SWEPT_FACE",FACE,{"disambiguationData":[OSD([sQuery(id+"F0.wireOp",EDGE,"E34")])]});
            var sketch = newSketch(context, id + "F10", { "sketchPlane" : qUnion([Q0])});
            skArc(sketch, "E201", {"start": v(3.71, 40.68) * mm, "mid": v(3.46, 40.7) * mm, "end": v(3.21, 40.72) * mm});
            skArc(sketch, "E202", {"start": v(4.79, 37.57) * mm, "mid": v(5.7, 36.2) * mm, "end": v(7.18, 35.48) * mm});
            skArc(sketch, "E203", {"start": v(3.21, 40.72) * mm, "mid": v(2.97, 40.74) * mm, "end": v(2.72, 40.76) * mm});
            skArc(sketch, "E204", {"start": v(-1.52, 36.17) * mm, "mid": v(0.05, 36.66) * mm, "end": v(1.17, 37.86) * mm});
            skLineSegment(sketch, "E205", {"start": v(4.79, 37.57) * mm, "end": v(4.58, 38.17) * mm});
            skLineSegment(sketch, "E206", {"start": v(1.17, 37.86) * mm, "end": v(1.52, 38.52) * mm});
            skLineSegment(sketch, "E207", {"start": v(1.52, 38.52) * mm, "end": v(2.72, 40.76) * mm});
            skLineSegment(sketch, "E208", {"start": v(4.58, 38.17) * mm, "end": v(3.71, 40.68) * mm});
            skArc(sketch, "E209.1.0", {"start": v(-10.13, 34.75) * mm, "mid": v(-8.73, 35.6) * mm, "end": v(-7.93, 37.04) * mm});
            skLineSegment(sketch, "E209.1.1", {"start": v(-7.93, 37.04) * mm, "end": v(-7.74, 37.76) * mm});
            skLineSegment(sketch, "E209.1.2", {"start": v(-7.74, 37.76) * mm, "end": v(-7.12, 40.23) * mm});
            skArc(sketch, "E209.1.3", {"start": v(-6.62, 40.3) * mm, "mid": v(-6.87, 40.27) * mm, "end": v(-7.12, 40.23) * mm});
            skArc(sketch, "E209.1.4", {"start": v(-6.13, 40.39) * mm, "mid": v(-6.38, 40.35) * mm, "end": v(-6.62, 40.3) * mm});
            skLineSegment(sketch, "E209.1.5", {"start": v(-4.68, 38.15) * mm, "end": v(-6.13, 40.39) * mm});
            skLineSegment(sketch, "E209.1.6", {"start": v(-4.34, 37.63) * mm, "end": v(-4.68, 38.15) * mm});
            skArc(sketch, "E209.1.7", {"start": v(-4.34, 37.63) * mm, "mid": v(-3.13, 36.52) * mm, "end": v(-1.52, 36.17) * mm});
            skArc(sketch, "E209.2.0", {"start": v(-18.16, 31.32) * mm, "mid": v(-17, 32.48) * mm, "end": v(-16.56, 34.06) * mm});
            skLineSegment(sketch, "E209.2.1", {"start": v(-16.56, 34.06) * mm, "end": v(-16.56, 34.8) * mm});
            skLineSegment(sketch, "E209.2.2", {"start": v(-16.56, 34.8) * mm, "end": v(-16.54, 37.35) * mm});
            skArc(sketch, "E209.2.3", {"start": v(-16.08, 37.55) * mm, "mid": v(-16.3, 37.45) * mm, "end": v(-16.54, 37.35) * mm});
            skArc(sketch, "E209.2.4", {"start": v(-15.62, 37.75) * mm, "mid": v(-15.85, 37.65) * mm, "end": v(-16.08, 37.55) * mm});
            skLineSegment(sketch, "E209.2.5", {"start": v(-13.68, 35.92) * mm, "end": v(-15.62, 37.75) * mm});
            skLineSegment(sketch, "E209.2.6", {"start": v(-13.22, 35.5) * mm, "end": v(-13.68, 35.92) * mm});
            skArc(sketch, "E209.2.7", {"start": v(-13.22, 35.5) * mm, "mid": v(-11.78, 34.71) * mm, "end": v(-10.13, 34.75) * mm});
            skArc(sketch, "E209.3.0", {"start": v(-25.12, 26.06) * mm, "mid": v(-24.27, 27.47) * mm, "end": v(-24.23, 29.11) * mm});
            skLineSegment(sketch, "E209.3.1", {"start": v(-24.23, 29.11) * mm, "end": v(-24.4, 29.84) * mm});
            skLineSegment(sketch, "E209.3.2", {"start": v(-24.4, 29.84) * mm, "end": v(-25, 32.3) * mm});
            skArc(sketch, "E209.3.3", {"start": v(-24.6, 32.61) * mm, "mid": v(-24.8, 32.46) * mm, "end": v(-25, 32.3) * mm});
            skArc(sketch, "E209.3.4", {"start": v(-24.2, 32.91) * mm, "mid": v(-24.4, 32.76) * mm, "end": v(-24.6, 32.61) * mm});
            skLineSegment(sketch, "E209.3.5", {"start": v(-21.88, 31.6) * mm, "end": v(-24.2, 32.91) * mm});
            skLineSegment(sketch, "E209.3.6", {"start": v(-21.33, 31.3) * mm, "end": v(-21.88, 31.6) * mm});
            skArc(sketch, "E209.3.7", {"start": v(-21.33, 31.3) * mm, "mid": v(-19.74, 30.89) * mm, "end": v(-18.16, 31.32) * mm});
            skArc(sketch, "E209.4.0", {"start": v(-30.63, 19.3) * mm, "mid": v(-30.14, 20.86) * mm, "end": v(-30.5, 22.47) * mm});
            skLineSegment(sketch, "E209.4.1", {"start": v(-30.5, 22.47) * mm, "end": v(-30.84, 23.13) * mm});
            skLineSegment(sketch, "E209.4.2", {"start": v(-30.84, 23.13) * mm, "end": v(-32, 25.39) * mm});
            skArc(sketch, "E209.4.3", {"start": v(-31.69, 25.78) * mm, "mid": v(-31.85, 25.58) * mm, "end": v(-32, 25.39) * mm});
            skArc(sketch, "E209.4.4", {"start": v(-31.37, 26.16) * mm, "mid": v(-31.53, 25.97) * mm, "end": v(-31.69, 25.78) * mm});
            skLineSegment(sketch, "E209.4.5", {"start": v(-28.8, 25.45) * mm, "end": v(-31.37, 26.16) * mm});
            skLineSegment(sketch, "E209.4.6", {"start": v(-28.2, 25.28) * mm, "end": v(-28.8, 25.45) * mm});
            skArc(sketch, "E209.4.7", {"start": v(-28.2, 25.28) * mm, "mid": v(-26.56, 25.26) * mm, "end": v(-25.12, 26.06) * mm});
            skArc(sketch, "E209.5.0", {"start": v(-34.36, 11.4) * mm, "mid": v(-34.26, 13.04) * mm, "end": v(-34.98, 14.51) * mm});
            skLineSegment(sketch, "E209.5.1", {"start": v(-34.98, 14.51) * mm, "end": v(-35.48, 15.08) * mm});
            skLineSegment(sketch, "E209.5.2", {"start": v(-35.48, 15.08) * mm, "end": v(-37.15, 17) * mm});
            skArc(sketch, "E209.5.3", {"start": v(-36.94, 17.45) * mm, "mid": v(-37.04, 17.22) * mm, "end": v(-37.15, 17) * mm});
            skArc(sketch, "E209.5.4", {"start": v(-36.72, 17.9) * mm, "mid": v(-36.83, 17.67) * mm, "end": v(-36.94, 17.45) * mm});
            skLineSegment(sketch, "E209.5.5", {"start": v(-34.06, 17.82) * mm, "end": v(-36.72, 17.9) * mm});
            skLineSegment(sketch, "E209.5.6", {"start": v(-33.43, 17.8) * mm, "end": v(-34.06, 17.82) * mm});
            skArc(sketch, "E209.5.7", {"start": v(-33.43, 17.8) * mm, "mid": v(-31.83, 18.17) * mm, "end": v(-30.63, 19.3) * mm});
            skArc(sketch, "E209.6.0", {"start": v(-36.09, 2.85) * mm, "mid": v(-36.38, 4.46) * mm, "end": v(-37.44, 5.72) * mm});
            skLineSegment(sketch, "E209.6.1", {"start": v(-37.44, 5.72) * mm, "end": v(-38.05, 6.15) * mm});
            skLineSegment(sketch, "E209.6.2", {"start": v(-38.05, 6.15) * mm, "end": v(-40.14, 7.6) * mm});
            skArc(sketch, "E209.6.3", {"start": v(-40.04, 8.1) * mm, "mid": v(-40.09, 7.85) * mm, "end": v(-40.14, 7.6) * mm});
            skArc(sketch, "E209.6.4", {"start": v(-39.94, 8.59) * mm, "mid": v(-39.99, 8.34) * mm, "end": v(-40.04, 8.1) * mm});
            skLineSegment(sketch, "E209.6.5", {"start": v(-37.34, 9.15) * mm, "end": v(-39.94, 8.59) * mm});
            skLineSegment(sketch, "E209.6.6", {"start": v(-36.72, 9.28) * mm, "end": v(-37.34, 9.15) * mm});
            skArc(sketch, "E209.6.7", {"start": v(-36.72, 9.28) * mm, "mid": v(-35.26, 10.03) * mm, "end": v(-34.36, 11.4) * mm});
            skArc(sketch, "E209.7.0", {"start": v(-35.72, -5.87) * mm, "mid": v(-36.4, -4.37) * mm, "end": v(-37.72, -3.4) * mm});
            skLineSegment(sketch, "E209.7.1", {"start": v(-37.72, -3.4) * mm, "end": v(-38.42, -3.14) * mm});
            skLineSegment(sketch, "E209.7.2", {"start": v(-38.42, -3.14) * mm, "end": v(-40.79, -2.22) * mm});
            skArc(sketch, "E209.7.3", {"start": v(-40.81, -1.72) * mm, "mid": v(-40.8, -1.97) * mm, "end": v(-40.79, -2.22) * mm});
            skArc(sketch, "E209.7.4", {"start": v(-40.83, -1.22) * mm, "mid": v(-40.82, -1.47) * mm, "end": v(-40.81, -1.72) * mm});
            skLineSegment(sketch, "E209.7.5", {"start": v(-38.44, -0.05) * mm, "end": v(-40.83, -1.22) * mm});
            skLineSegment(sketch, "E209.7.6", {"start": v(-37.88, 0.22) * mm, "end": v(-38.44, -0.05) * mm});
            skArc(sketch, "E209.7.7", {"start": v(-37.88, 0.22) * mm, "mid": v(-36.63, 1.3) * mm, "end": v(-36.09, 2.85) * mm});
            skArc(sketch, "E209.8.0", {"start": v(-33.28, -14.25) * mm, "mid": v(-34.3, -12.96) * mm, "end": v(-35.81, -12.33) * mm});
            skLineSegment(sketch, "E209.8.1", {"start": v(-35.81, -12.33) * mm, "end": v(-36.55, -12.24) * mm});
            skLineSegment(sketch, "E209.8.2", {"start": v(-36.55, -12.24) * mm, "end": v(-39.07, -11.91) * mm});
            skArc(sketch, "E209.8.3", {"start": v(-39.22, -11.44) * mm, "mid": v(-39.15, -11.67) * mm, "end": v(-39.07, -11.91) * mm});
            skArc(sketch, "E209.8.4", {"start": v(-39.35, -10.95) * mm, "mid": v(-39.29, -11.2) * mm, "end": v(-39.22, -11.44) * mm});
            skLineSegment(sketch, "E209.8.5", {"start": v(-37.31, -9.25) * mm, "end": v(-39.35, -10.95) * mm});
            skLineSegment(sketch, "E209.8.6", {"start": v(-36.83, -8.85) * mm, "end": v(-37.31, -9.25) * mm});
            skArc(sketch, "E209.8.7", {"start": v(-36.83, -8.85) * mm, "mid": v(-35.88, -7.5) * mm, "end": v(-35.72, -5.87) * mm});
            skArc(sketch, "E209.9.0", {"start": v(-28.9, -21.8) * mm, "mid": v(-30.2, -20.78) * mm, "end": v(-31.82, -20.55) * mm});
            skLineSegment(sketch, "E209.9.1", {"start": v(-31.82, -20.55) * mm, "end": v(-32.56, -20.63) * mm});
            skLineSegment(sketch, "E209.9.2", {"start": v(-32.56, -20.63) * mm, "end": v(-35.09, -20.92) * mm});
            skArc(sketch, "E209.9.3", {"start": v(-35.34, -20.49) * mm, "mid": v(-35.21, -20.7) * mm, "end": v(-35.09, -20.92) * mm});
            skArc(sketch, "E209.9.4", {"start": v(-35.59, -20.05) * mm, "mid": v(-35.47, -20.27) * mm, "end": v(-35.34, -20.49) * mm});
            skLineSegment(sketch, "E209.9.5", {"start": v(-34.01, -17.9) * mm, "end": v(-35.59, -20.05) * mm});
            skLineSegment(sketch, "E209.9.6", {"start": v(-33.64, -17.4) * mm, "end": v(-34.01, -17.9) * mm});
            skArc(sketch, "E209.9.7", {"start": v(-33.64, -17.4) * mm, "mid": v(-33.04, -15.87) * mm, "end": v(-33.28, -14.25) * mm});
            skArc(sketch, "E209.10.0", {"start": v(-22.84, -28.08) * mm, "mid": v(-24.34, -27.4) * mm, "end": v(-25.98, -27.56) * mm});
            skLineSegment(sketch, "E209.10.1", {"start": v(-25.98, -27.56) * mm, "end": v(-26.68, -27.82) * mm});
            skLineSegment(sketch, "E209.10.2", {"start": v(-26.68, -27.82) * mm, "end": v(-29.06, -28.7) * mm});
            skArc(sketch, "E209.10.3", {"start": v(-29.41, -28.35) * mm, "mid": v(-29.24, -28.53) * mm, "end": v(-29.06, -28.7) * mm});
            skArc(sketch, "E209.10.4", {"start": v(-29.76, -27.99) * mm, "mid": v(-29.58, -28.17) * mm, "end": v(-29.41, -28.35) * mm});
            skLineSegment(sketch, "E209.10.5", {"start": v(-28.74, -25.53) * mm, "end": v(-29.76, -27.99) * mm});
            skLineSegment(sketch, "E209.10.6", {"start": v(-28.5, -24.95) * mm, "end": v(-28.74, -25.53) * mm});
            skArc(sketch, "E209.10.7", {"start": v(-28.5, -24.95) * mm, "mid": v(-28.28, -23.32) * mm, "end": v(-28.9, -21.8) * mm});
            skArc(sketch, "E209.11.0", {"start": v(-15.46, -32.73) * mm, "mid": v(-17.08, -32.44) * mm, "end": v(-18.63, -32.98) * mm});
            skLineSegment(sketch, "E209.11.1", {"start": v(-18.63, -32.98) * mm, "end": v(-19.24, -33.4) * mm});
            skLineSegment(sketch, "E209.11.2", {"start": v(-19.24, -33.4) * mm, "end": v(-21.35, -34.83) * mm});
            skArc(sketch, "E209.11.3", {"start": v(-21.77, -34.56) * mm, "mid": v(-21.56, -34.7) * mm, "end": v(-21.35, -34.83) * mm});
            skArc(sketch, "E209.11.4", {"start": v(-22.2, -34.3) * mm, "mid": v(-21.98, -34.43) * mm, "end": v(-21.77, -34.56) * mm});
            skLineSegment(sketch, "E209.11.5", {"start": v(-21.8, -31.66) * mm, "end": v(-22.2, -34.3) * mm});
            skLineSegment(sketch, "E209.11.6", {"start": v(-21.7, -31.04) * mm, "end": v(-21.8, -31.66) * mm});
            skArc(sketch, "E209.11.7", {"start": v(-21.7, -31.04) * mm, "mid": v(-21.88, -29.41) * mm, "end": v(-22.84, -28.08) * mm});
            skArc(sketch, "E209.12.0", {"start": v(-7.18, -35.48) * mm, "mid": v(-8.82, -35.58) * mm, "end": v(-10.2, -36.48) * mm});
            skLineSegment(sketch, "E209.12.1", {"start": v(-10.2, -36.48) * mm, "end": v(-10.7, -37.03) * mm});
            skLineSegment(sketch, "E209.12.2", {"start": v(-10.7, -37.03) * mm, "end": v(-12.4, -38.93) * mm});
            skArc(sketch, "E209.12.3", {"start": v(-12.87, -38.77) * mm, "mid": v(-12.63, -38.85) * mm, "end": v(-12.4, -38.93) * mm});
            skArc(sketch, "E209.12.4", {"start": v(-13.34, -38.61) * mm, "mid": v(-13.1, -38.7) * mm, "end": v(-12.87, -38.77) * mm});
            skLineSegment(sketch, "E209.12.5", {"start": v(-13.58, -35.96) * mm, "end": v(-13.34, -38.61) * mm});
            skLineSegment(sketch, "E209.12.6", {"start": v(-13.64, -35.33) * mm, "end": v(-13.58, -35.96) * mm});
            skArc(sketch, "E209.12.7", {"start": v(-13.64, -35.33) * mm, "mid": v(-14.2, -33.8) * mm, "end": v(-15.46, -32.73) * mm});
            skArc(sketch, "E209.13.0", {"start": v(1.52, -36.17) * mm, "mid": v(-0.05, -36.66) * mm, "end": v(-1.17, -37.86) * mm});
            skLineSegment(sketch, "E209.13.1", {"start": v(-1.17, -37.86) * mm, "end": v(-1.52, -38.52) * mm});
            skLineSegment(sketch, "E209.13.2", {"start": v(-1.52, -38.52) * mm, "end": v(-2.72, -40.76) * mm});
            skArc(sketch, "E209.13.3", {"start": v(-3.21, -40.72) * mm, "mid": v(-2.97, -40.74) * mm, "end": v(-2.72, -40.76) * mm});
            skArc(sketch, "E209.13.4", {"start": v(-3.71, -40.68) * mm, "mid": v(-3.46, -40.7) * mm, "end": v(-3.21, -40.72) * mm});
            skLineSegment(sketch, "E209.13.5", {"start": v(-4.58, -38.17) * mm, "end": v(-3.71, -40.68) * mm});
            skLineSegment(sketch, "E209.13.6", {"start": v(-4.79, -37.57) * mm, "end": v(-4.58, -38.17) * mm});
            skArc(sketch, "E209.13.7", {"start": v(-4.79, -37.57) * mm, "mid": v(-5.7, -36.2) * mm, "end": v(-7.18, -35.48) * mm});
            skArc(sketch, "E209.14.0", {"start": v(10.13, -34.75) * mm, "mid": v(8.73, -35.6) * mm, "end": v(7.93, -37.04) * mm});
            skLineSegment(sketch, "E209.14.1", {"start": v(7.93, -37.04) * mm, "end": v(7.74, -37.76) * mm});
            skLineSegment(sketch, "E209.14.2", {"start": v(7.74, -37.76) * mm, "end": v(7.12, -40.23) * mm});
            skArc(sketch, "E209.14.3", {"start": v(6.62, -40.3) * mm, "mid": v(6.87, -40.27) * mm, "end": v(7.12, -40.23) * mm});
            skArc(sketch, "E209.14.4", {"start": v(6.13, -40.39) * mm, "mid": v(6.38, -40.35) * mm, "end": v(6.62, -40.3) * mm});
            skLineSegment(sketch, "E209.14.5", {"start": v(4.68, -38.15) * mm, "end": v(6.13, -40.39) * mm});
            skLineSegment(sketch, "E209.14.6", {"start": v(4.34, -37.63) * mm, "end": v(4.68, -38.15) * mm});
            skArc(sketch, "E209.14.7", {"start": v(4.34, -37.63) * mm, "mid": v(3.13, -36.52) * mm, "end": v(1.52, -36.17) * mm});
            skArc(sketch, "E209.15.0", {"start": v(18.16, -31.32) * mm, "mid": v(17, -32.48) * mm, "end": v(16.56, -34.06) * mm});
            skLineSegment(sketch, "E209.15.1", {"start": v(16.56, -34.06) * mm, "end": v(16.56, -34.8) * mm});
            skLineSegment(sketch, "E209.15.2", {"start": v(16.56, -34.8) * mm, "end": v(16.54, -37.35) * mm});
            skArc(sketch, "E209.15.3", {"start": v(16.08, -37.55) * mm, "mid": v(16.3, -37.45) * mm, "end": v(16.54, -37.35) * mm});
            skArc(sketch, "E209.15.4", {"start": v(15.62, -37.75) * mm, "mid": v(15.85, -37.65) * mm, "end": v(16.08, -37.55) * mm});
            skLineSegment(sketch, "E209.15.5", {"start": v(13.68, -35.92) * mm, "end": v(15.62, -37.75) * mm});
            skLineSegment(sketch, "E209.15.6", {"start": v(13.22, -35.5) * mm, "end": v(13.68, -35.92) * mm});
            skArc(sketch, "E209.15.7", {"start": v(13.22, -35.5) * mm, "mid": v(11.78, -34.71) * mm, "end": v(10.13, -34.75) * mm});
            skArc(sketch, "E209.16.0", {"start": v(25.12, -26.06) * mm, "mid": v(24.27, -27.47) * mm, "end": v(24.23, -29.11) * mm});
            skLineSegment(sketch, "E209.16.1", {"start": v(24.23, -29.11) * mm, "end": v(24.4, -29.84) * mm});
            skLineSegment(sketch, "E209.16.2", {"start": v(24.4, -29.84) * mm, "end": v(25, -32.3) * mm});
            skArc(sketch, "E209.16.3", {"start": v(24.6, -32.61) * mm, "mid": v(24.8, -32.46) * mm, "end": v(25, -32.3) * mm});
            skArc(sketch, "E209.16.4", {"start": v(24.2, -32.91) * mm, "mid": v(24.4, -32.76) * mm, "end": v(24.6, -32.61) * mm});
            skLineSegment(sketch, "E209.16.5", {"start": v(21.88, -31.6) * mm, "end": v(24.2, -32.91) * mm});
            skLineSegment(sketch, "E209.16.6", {"start": v(21.33, -31.3) * mm, "end": v(21.88, -31.6) * mm});
            skArc(sketch, "E209.16.7", {"start": v(21.33, -31.3) * mm, "mid": v(19.74, -30.89) * mm, "end": v(18.16, -31.32) * mm});
            skArc(sketch, "E209.17.0", {"start": v(30.63, -19.3) * mm, "mid": v(30.14, -20.86) * mm, "end": v(30.5, -22.47) * mm});
            skLineSegment(sketch, "E209.17.1", {"start": v(30.5, -22.47) * mm, "end": v(30.84, -23.13) * mm});
            skLineSegment(sketch, "E209.17.2", {"start": v(30.84, -23.13) * mm, "end": v(32, -25.39) * mm});
            skArc(sketch, "E209.17.3", {"start": v(31.69, -25.78) * mm, "mid": v(31.85, -25.58) * mm, "end": v(32, -25.39) * mm});
            skArc(sketch, "E209.17.4", {"start": v(31.37, -26.16) * mm, "mid": v(31.53, -25.97) * mm, "end": v(31.69, -25.78) * mm});
            skLineSegment(sketch, "E209.17.5", {"start": v(28.8, -25.45) * mm, "end": v(31.37, -26.16) * mm});
            skLineSegment(sketch, "E209.17.6", {"start": v(28.2, -25.28) * mm, "end": v(28.8, -25.45) * mm});
            skArc(sketch, "E209.17.7", {"start": v(28.2, -25.28) * mm, "mid": v(26.56, -25.26) * mm, "end": v(25.12, -26.06) * mm});
            skArc(sketch, "E209.18.0", {"start": v(34.36, -11.4) * mm, "mid": v(34.26, -13.04) * mm, "end": v(34.98, -14.51) * mm});
            skLineSegment(sketch, "E209.18.1", {"start": v(34.98, -14.51) * mm, "end": v(35.48, -15.08) * mm});
            skLineSegment(sketch, "E209.18.2", {"start": v(35.48, -15.08) * mm, "end": v(37.15, -17) * mm});
            skArc(sketch, "E209.18.3", {"start": v(36.94, -17.45) * mm, "mid": v(37.04, -17.22) * mm, "end": v(37.15, -17) * mm});
            skArc(sketch, "E209.18.4", {"start": v(36.72, -17.9) * mm, "mid": v(36.83, -17.67) * mm, "end": v(36.94, -17.45) * mm});
            skLineSegment(sketch, "E209.18.5", {"start": v(34.06, -17.82) * mm, "end": v(36.72, -17.9) * mm});
            skLineSegment(sketch, "E209.18.6", {"start": v(33.43, -17.8) * mm, "end": v(34.06, -17.82) * mm});
            skArc(sketch, "E209.18.7", {"start": v(33.43, -17.8) * mm, "mid": v(31.83, -18.17) * mm, "end": v(30.63, -19.3) * mm});
            skArc(sketch, "E209.19.0", {"start": v(36.09, -2.85) * mm, "mid": v(36.38, -4.46) * mm, "end": v(37.44, -5.72) * mm});
            skLineSegment(sketch, "E209.19.1", {"start": v(37.44, -5.72) * mm, "end": v(38.05, -6.15) * mm});
            skLineSegment(sketch, "E209.19.2", {"start": v(38.05, -6.15) * mm, "end": v(40.14, -7.6) * mm});
            skArc(sketch, "E209.19.3", {"start": v(40.04, -8.1) * mm, "mid": v(40.09, -7.85) * mm, "end": v(40.14, -7.6) * mm});
            skArc(sketch, "E209.19.4", {"start": v(39.94, -8.59) * mm, "mid": v(39.99, -8.34) * mm, "end": v(40.04, -8.1) * mm});
            skLineSegment(sketch, "E209.19.5", {"start": v(37.34, -9.15) * mm, "end": v(39.94, -8.59) * mm});
            skLineSegment(sketch, "E209.19.6", {"start": v(36.72, -9.28) * mm, "end": v(37.34, -9.15) * mm});
            skArc(sketch, "E209.19.7", {"start": v(36.72, -9.28) * mm, "mid": v(35.26, -10.03) * mm, "end": v(34.36, -11.4) * mm});
            skArc(sketch, "E209.20.0", {"start": v(35.72, 5.87) * mm, "mid": v(36.4, 4.37) * mm, "end": v(37.72, 3.4) * mm});
            skLineSegment(sketch, "E209.20.1", {"start": v(37.72, 3.4) * mm, "end": v(38.42, 3.14) * mm});
            skLineSegment(sketch, "E209.20.2", {"start": v(38.42, 3.14) * mm, "end": v(40.79, 2.22) * mm});
            skArc(sketch, "E209.20.3", {"start": v(40.81, 1.72) * mm, "mid": v(40.8, 1.97) * mm, "end": v(40.79, 2.22) * mm});
            skArc(sketch, "E209.20.4", {"start": v(40.83, 1.22) * mm, "mid": v(40.82, 1.47) * mm, "end": v(40.81, 1.72) * mm});
            skLineSegment(sketch, "E209.20.5", {"start": v(38.44, 0.05) * mm, "end": v(40.83, 1.22) * mm});
            skLineSegment(sketch, "E209.20.6", {"start": v(37.88, -0.22) * mm, "end": v(38.44, 0.05) * mm});
            skArc(sketch, "E209.20.7", {"start": v(37.88, -0.22) * mm, "mid": v(36.63, -1.3) * mm, "end": v(36.09, -2.85) * mm});
            skArc(sketch, "E209.21.0", {"start": v(33.28, 14.25) * mm, "mid": v(34.3, 12.96) * mm, "end": v(35.81, 12.33) * mm});
            skLineSegment(sketch, "E209.21.1", {"start": v(35.81, 12.33) * mm, "end": v(36.55, 12.24) * mm});
            skLineSegment(sketch, "E209.21.2", {"start": v(36.55, 12.24) * mm, "end": v(39.07, 11.91) * mm});
            skArc(sketch, "E209.21.3", {"start": v(39.22, 11.44) * mm, "mid": v(39.15, 11.67) * mm, "end": v(39.07, 11.91) * mm});
            skArc(sketch, "E209.21.4", {"start": v(39.35, 10.95) * mm, "mid": v(39.29, 11.2) * mm, "end": v(39.22, 11.44) * mm});
            skLineSegment(sketch, "E209.21.5", {"start": v(37.31, 9.25) * mm, "end": v(39.35, 10.95) * mm});
            skLineSegment(sketch, "E209.21.6", {"start": v(36.83, 8.85) * mm, "end": v(37.31, 9.25) * mm});
            skArc(sketch, "E209.21.7", {"start": v(36.83, 8.85) * mm, "mid": v(35.88, 7.5) * mm, "end": v(35.72, 5.87) * mm});
            skArc(sketch, "E209.22.0", {"start": v(28.9, 21.8) * mm, "mid": v(30.2, 20.78) * mm, "end": v(31.82, 20.55) * mm});
            skLineSegment(sketch, "E209.22.1", {"start": v(31.82, 20.55) * mm, "end": v(32.56, 20.63) * mm});
            skLineSegment(sketch, "E209.22.2", {"start": v(32.56, 20.63) * mm, "end": v(35.09, 20.92) * mm});
            skArc(sketch, "E209.22.3", {"start": v(35.34, 20.49) * mm, "mid": v(35.21, 20.7) * mm, "end": v(35.09, 20.92) * mm});
            skArc(sketch, "E209.22.4", {"start": v(35.59, 20.05) * mm, "mid": v(35.47, 20.27) * mm, "end": v(35.34, 20.49) * mm});
            skLineSegment(sketch, "E209.22.5", {"start": v(34.01, 17.9) * mm, "end": v(35.59, 20.05) * mm});
            skLineSegment(sketch, "E209.22.6", {"start": v(33.64, 17.4) * mm, "end": v(34.01, 17.9) * mm});
            skArc(sketch, "E209.22.7", {"start": v(33.64, 17.4) * mm, "mid": v(33.04, 15.87) * mm, "end": v(33.28, 14.25) * mm});
            skArc(sketch, "E209.23.0", {"start": v(22.84, 28.08) * mm, "mid": v(24.34, 27.4) * mm, "end": v(25.98, 27.56) * mm});
            skLineSegment(sketch, "E209.23.1", {"start": v(25.98, 27.56) * mm, "end": v(26.68, 27.82) * mm});
            skLineSegment(sketch, "E209.23.2", {"start": v(26.68, 27.82) * mm, "end": v(29.06, 28.7) * mm});
            skArc(sketch, "E209.23.3", {"start": v(29.41, 28.35) * mm, "mid": v(29.24, 28.53) * mm, "end": v(29.06, 28.7) * mm});
            skArc(sketch, "E209.23.4", {"start": v(29.76, 27.99) * mm, "mid": v(29.58, 28.17) * mm, "end": v(29.41, 28.35) * mm});
            skLineSegment(sketch, "E209.23.5", {"start": v(28.74, 25.53) * mm, "end": v(29.76, 27.99) * mm});
            skLineSegment(sketch, "E209.23.6", {"start": v(28.5, 24.95) * mm, "end": v(28.74, 25.53) * mm});
            skArc(sketch, "E209.23.7", {"start": v(28.5, 24.95) * mm, "mid": v(28.28, 23.32) * mm, "end": v(28.9, 21.8) * mm});
            skArc(sketch, "E209.24.0", {"start": v(15.46, 32.73) * mm, "mid": v(17.08, 32.44) * mm, "end": v(18.63, 32.98) * mm});
            skLineSegment(sketch, "E209.24.1", {"start": v(18.63, 32.98) * mm, "end": v(19.24, 33.4) * mm});
            skLineSegment(sketch, "E209.24.2", {"start": v(19.24, 33.4) * mm, "end": v(21.35, 34.83) * mm});
            skArc(sketch, "E209.24.3", {"start": v(21.77, 34.56) * mm, "mid": v(21.56, 34.7) * mm, "end": v(21.35, 34.83) * mm});
            skArc(sketch, "E209.24.4", {"start": v(22.2, 34.3) * mm, "mid": v(21.98, 34.43) * mm, "end": v(21.77, 34.56) * mm});
            skLineSegment(sketch, "E209.24.5", {"start": v(21.8, 31.66) * mm, "end": v(22.2, 34.3) * mm});
            skLineSegment(sketch, "E209.24.6", {"start": v(21.7, 31.04) * mm, "end": v(21.8, 31.66) * mm});
            skArc(sketch, "E209.24.7", {"start": v(21.7, 31.04) * mm, "mid": v(21.88, 29.41) * mm, "end": v(22.84, 28.08) * mm});
            skArc(sketch, "E209.25.0", {"start": v(7.18, 35.48) * mm, "mid": v(8.82, 35.58) * mm, "end": v(10.2, 36.48) * mm});
            skLineSegment(sketch, "E209.25.1", {"start": v(10.2, 36.48) * mm, "end": v(10.7, 37.03) * mm});
            skLineSegment(sketch, "E209.25.2", {"start": v(10.7, 37.03) * mm, "end": v(12.4, 38.93) * mm});
            skArc(sketch, "E209.25.3", {"start": v(12.87, 38.77) * mm, "mid": v(12.63, 38.85) * mm, "end": v(12.4, 38.93) * mm});
            skArc(sketch, "E209.25.4", {"start": v(13.34, 38.61) * mm, "mid": v(13.1, 38.7) * mm, "end": v(12.87, 38.77) * mm});
            skLineSegment(sketch, "E209.25.5", {"start": v(13.58, 35.96) * mm, "end": v(13.34, 38.61) * mm});
            skLineSegment(sketch, "E209.25.6", {"start": v(13.64, 35.33) * mm, "end": v(13.58, 35.96) * mm});
            skArc(sketch, "E209.25.7", {"start": v(13.64, 35.33) * mm, "mid": v(14.2, 33.8) * mm, "end": v(15.46, 32.73) * mm});
            skCircle(sketch, "E210", {"center": v(0, 0) * mm, "radius": 43.2 * mm});
            skSolve(sketch);
        }
        {
            var Q0;
            Q0=makeQuery(id+"F10.imprint","IMPRINT",FACE,{"disambiguationData":[TD([[makeQuery(id+"F10.imprint","IMPRINT",EDGE,{"derivedFrom":sQuery(id+"F10.wireOp",EDGE,"E201")}),-1.0]])]});
            extrude(context, id + "F11", {"entities" : qUnion([Q0]), "operationType" : NewBodyOperationType.REMOVE, "oppositeDirection" : true, "depth" : 6 * mm, "offsetDistance" : 25 * mm});
        }
    });
